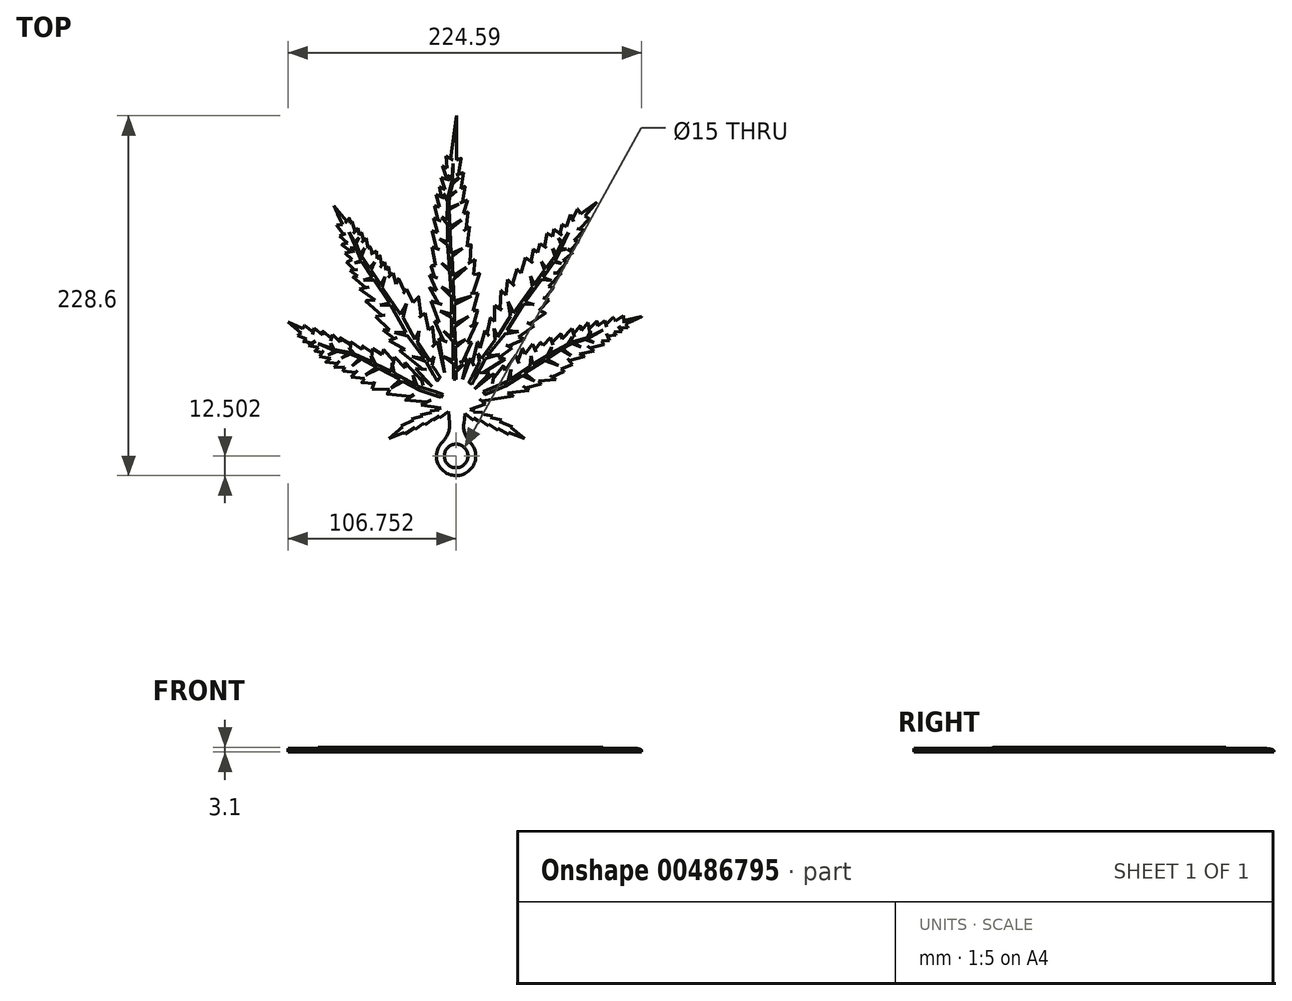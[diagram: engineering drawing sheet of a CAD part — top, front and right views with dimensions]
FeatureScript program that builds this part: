
annotation { "Feature Type Name" : "Feature", "Feature Type Description" : "" }
export const myFeature = defineFeature(function(context is Context, id is Id, definition is map)
    precondition{}
    {
        {
            var Q0;
            Q0=qCreatedBy(makeId("Top.planeOp"),FACE);
            cPlane(context, id + "F0", {"entities" : qUnion([Q0]), "cplaneType" : CPlaneType.OFFSET, "offset" : 2.5 * mm, "width" : 150 * mm, "height" : 150 * mm});
        }
        {
            var Q0;
            Q0=qCreatedBy(makeId("Top.planeOp"),FACE);
            var sketch = newSketch(context, id + "F1", { "sketchPlane" : qUnion([Q0])});
            skLineSegment(sketch, "E0.MirrorCS", {"start": v(-24.15, -17.47) * mm, "end": v(-22.78, -18.23) * mm});
            skLineSegment(sketch, "E1.MirrorCS", {"start": v(-21.88, -22.85) * mm, "end": v(-21.43, -23.84) * mm});
            skLineSegment(sketch, "E2.MirrorCS", {"start": v(-16.34, -20.03) * mm, "end": v(-16.15, -20.85) * mm});
            skLineSegment(sketch, "E3.MirrorCS", {"start": v(-27.7, -25.52) * mm, "end": v(-27.51, -26.67) * mm});
            skLineSegment(sketch, "E4.MirrorCS", {"start": v(-16.15, -20.85) * mm, "end": v(-12.07, -18.38) * mm});
            skLineSegment(sketch, "E5.MirrorCS", {"start": v(-29.84, -20.19) * mm, "end": v(-28.49, -20.94) * mm});
            skLineSegment(sketch, "E6.MirrorCS", {"start": v(-27.51, -26.67) * mm, "end": v(-21.88, -22.85) * mm});
            skLineSegment(sketch, "E7.MirrorCS", {"start": v(-17.1, -16.14) * mm, "end": v(-24.15, -17.47) * mm});
            skLineSegment(sketch, "E8.MirrorCS", {"start": v(93.66, 39.93) * mm, "end": v(93.13, 42.28) * mm});
            skLineSegment(sketch, "E9.MirrorCS", {"start": v(-18.21, -15.02) * mm, "end": v(-17.1, -16.14) * mm});
            skLineSegment(sketch, "E10.MirrorCS", {"start": v(-12.36, -14.52) * mm, "end": v(-18.21, -15.02) * mm});
            skLineSegment(sketch, "E11.MirrorCS", {"start": v(-21.43, -23.84) * mm, "end": v(-16.34, -20.03) * mm});
            skLineSegment(sketch, "E12.MirrorCS", {"start": v(99.9, 33.33) * mm, "end": v(98.7, 35) * mm});
            skLineSegment(sketch, "E13.MirrorCS", {"start": v(-22.78, -18.23) * mm, "end": v(-29.84, -20.19) * mm});
            skLineSegment(sketch, "E14.MirrorCS", {"start": v(9.62, -15.66) * mm, "end": v(10.2, -14.93) * mm});
            skLineSegment(sketch, "E15.MirrorCS", {"start": v(48.5, 23.9) * mm, "end": v(46.84, 27.4) * mm});
            skLineSegment(sketch, "E16.MirrorCS", {"start": v(-8.6, 125.55) * mm, "end": v(-12.12, 127.28) * mm});
            skLineSegment(sketch, "E17.MirrorCS", {"start": v(88.27, 39.04) * mm, "end": v(88, 42) * mm});
            skLineSegment(sketch, "E18.MirrorCS", {"start": v(-12.07, -18.38) * mm, "end": v(-12.07, -19.6) * mm});
            skLineSegment(sketch, "E19.MirrorCS", {"start": v(-44.52, 76.69) * mm, "end": v(-46.07, 74.38) * mm});
            skLineSegment(sketch, "E20.MirrorCS", {"start": v(14.51, -17.11) * mm, "end": v(15.3, -16.07) * mm});
            skLineSegment(sketch, "E21.MirrorCS", {"start": v(-39.89, 65.56) * mm, "end": v(-41.74, 72.67) * mm});
            skLineSegment(sketch, "E22.MirrorCS", {"start": v(93.13, 42.28) * mm, "end": v(88.27, 39.04) * mm});
            skLineSegment(sketch, "E23.MirrorCS", {"start": v(-12.07, -19.6) * mm, "end": v(-6.3, -15.51) * mm});
            skLineSegment(sketch, "E24.MirrorCS", {"start": v(88, 42) * mm, "end": v(82.7, 37.15) * mm});
            skLineSegment(sketch, "E25.MirrorCS", {"start": v(-47.18, 79.6) * mm, "end": v(-48.77, 77.58) * mm});
            skLineSegment(sketch, "E26.MirrorCS", {"start": v(99.75, 42.07) * mm, "end": v(98.19, 44.3) * mm});
            skLineSegment(sketch, "E27.MirrorCS", {"start": v(-63.23, 96.82) * mm, "end": v(-63.82, 101.24) * mm});
            skLineSegment(sketch, "E28.MirrorCS", {"start": v(-12.95, -13.9) * mm, "end": v(-12.36, -14.52) * mm});
            skLineSegment(sketch, "E29.MirrorCS", {"start": v(-67.78, 81.08) * mm, "end": v(-71.02, 79.47) * mm});
            skLineSegment(sketch, "E30.MirrorCS", {"start": v(95.95, 29.74) * mm, "end": v(94.6, 32.57) * mm});
            skLineSegment(sketch, "E31.MirrorCS", {"start": v(98.19, 44.3) * mm, "end": v(93.66, 39.93) * mm});
            skLineSegment(sketch, "E32.MirrorCS", {"start": v(-60.85, 26.35) * mm, "end": v(-61.4, 24) * mm});
            skLineSegment(sketch, "E33.MirrorCS", {"start": v(98.7, 35) * mm, "end": v(103.85, 35.51) * mm});
            skLineSegment(sketch, "E34.MirrorCS", {"start": v(-52.13, 86.53) * mm, "end": v(-54.6, 85.35) * mm});
            skLineSegment(sketch, "E35.MirrorCS", {"start": v(-57.39, 88.4) * mm, "end": v(-58.72, 94.78) * mm});
            skLineSegment(sketch, "E36.MirrorCS", {"start": v(-96.6, 30.56) * mm, "end": v(-98.6, 28.98) * mm});
            skLineSegment(sketch, "E37.MirrorCS", {"start": v(-23.87, -11.37) * mm, "end": v(-7.76, -13.63) * mm});
            skLineSegment(sketch, "E38.MirrorCS", {"start": v(59.47, 28.52) * mm, "end": v(58.4, 31.74) * mm});
            skLineSegment(sketch, "E39.MirrorCS", {"start": v(22.79, 41.65) * mm, "end": v(20.2, 44.17) * mm});
            skLineSegment(sketch, "E40.MirrorCS", {"start": v(-91.93, 37.8) * mm, "end": v(-92.53, 35.19) * mm});
            skLineSegment(sketch, "E41.MirrorCS", {"start": v(-8.17, -11.87) * mm, "end": v(-12.95, -13.9) * mm});
            skLineSegment(sketch, "E42.MirrorCS", {"start": v(94.6, 32.57) * mm, "end": v(99.9, 33.33) * mm});
            skLineSegment(sketch, "E43.MirrorCS", {"start": v(-70.5, 91.5) * mm, "end": v(-74.2, 90.73) * mm});
            skLineSegment(sketch, "E44.MirrorCS", {"start": v(40.63, 24.63) * mm, "end": v(37.6, 16.9) * mm});
            skLineSegment(sketch, "E45.MirrorCS", {"start": v(-67.78, 105.17) * mm, "end": v(-68.8, 104.3) * mm});
            skLineSegment(sketch, "E46.MirrorCS", {"start": v(9.47, -20.96) * mm, "end": v(9.47, -19.45) * mm});
            skLineSegment(sketch, "E47.MirrorCS", {"start": v(-69.45, 107.55) * mm, "end": v(-71.09, 105.54) * mm});
            skLineSegment(sketch, "E48.MirrorCS", {"start": v(107.5, 38.06) * mm, "end": v(106.14, 40.04) * mm});
            skLineSegment(sketch, "E49.MirrorCS", {"start": v(-49.84, 83.5) * mm, "end": v(-51.68, 81.6) * mm});
            skLineSegment(sketch, "E50.MirrorCS", {"start": v(59.63, 95.72) * mm, "end": v(56.23, 97.8) * mm});
            skLineSegment(sketch, "E51.MirrorCS", {"start": v(-11, 121.03) * mm, "end": v(-14.22, 122.51) * mm});
            skLineSegment(sketch, "E52.MirrorCS", {"start": v(-12.12, 127.28) * mm, "end": v(-11, 121.03) * mm});
            skLineSegment(sketch, "E53.MirrorCS", {"start": v(-54.6, 85.35) * mm, "end": v(-56.09, 89.21) * mm});
            skLineSegment(sketch, "E54.MirrorCS", {"start": v(-65.77, 98.92) * mm, "end": v(-67.78, 105.17) * mm});
            skLineSegment(sketch, "E55.MirrorCS", {"start": v(10.2, -14.93) * mm, "end": v(5.27, -13.6) * mm});
            skLineSegment(sketch, "E56.MirrorCS", {"start": v(-46.07, 74.38) * mm, "end": v(-47.18, 79.6) * mm});
            skLineSegment(sketch, "E57.MirrorCS", {"start": v(53.77, 26.64) * mm, "end": v(52.16, 28.56) * mm});
            skLineSegment(sketch, "E58.MirrorCS", {"start": v(-79.9, 33.62) * mm, "end": v(-80.8, 30.9) * mm});
            skLineSegment(sketch, "E59.MirrorCS", {"start": v(33.94, 24.96) * mm, "end": v(31.73, 26.08) * mm});
            skLineSegment(sketch, "E60.MirrorCS", {"start": v(-68.18, 86.24) * mm, "end": v(-72.2, 85.35) * mm});
            skLineSegment(sketch, "E61.MirrorCS", {"start": v(-63.82, 101.24) * mm, "end": v(-65.77, 98.92) * mm});
            skLineSegment(sketch, "E62.MirrorCS", {"start": v(36.08, 20.08) * mm, "end": v(29.34, 10.62) * mm});
            skLineSegment(sketch, "E63.MirrorCS", {"start": v(-54.6, 24.71) * mm, "end": v(-54.85, 22.2) * mm});
            skLineSegment(sketch, "E64.MirrorCS", {"start": v(52.16, 28.56) * mm, "end": v(48.5, 23.9) * mm});
            skLineSegment(sketch, "E65.MirrorCS", {"start": v(-61.69, 98.18) * mm, "end": v(-63.23, 96.82) * mm});
            skLineSegment(sketch, "E66.MirrorCS", {"start": v(-54.85, 22.2) * mm, "end": v(-60.85, 26.35) * mm});
            skLineSegment(sketch, "E67.MirrorCS", {"start": v(-68.77, 28.98) * mm, "end": v(-68.77, 27) * mm});
            skLineSegment(sketch, "E68.MirrorCS", {"start": v(-68.77, 27) * mm, "end": v(-75.14, 31.33) * mm});
            skLineSegment(sketch, "E69.MirrorCS", {"start": v(11.68, 41.54) * mm, "end": v(9.37, 39.84) * mm});
            skLineSegment(sketch, "E70.MirrorCS", {"start": v(-10.18, 140.6) * mm, "end": v(-7.4, 132) * mm});
            skLineSegment(sketch, "E71.MirrorCS", {"start": v(-77.58, 102.97) * mm, "end": v(-73.13, 97.13) * mm});
            skLineSegment(sketch, "E72.MirrorCS", {"start": v(90.7, 29.27) * mm, "end": v(95.95, 29.74) * mm});
            skLineSegment(sketch, "E73.MirrorCS", {"start": v(-92.53, 35.19) * mm, "end": v(-97.83, 39.3) * mm});
            skLineSegment(sketch, "E74.MirrorCS", {"start": v(-74.2, 90.73) * mm, "end": v(-68.18, 86.24) * mm});
            skLineSegment(sketch, "E75.MirrorCS", {"start": v(15.3, -16.07) * mm, "end": v(9.62, -15.66) * mm});
            skLineSegment(sketch, "E76.MirrorCS", {"start": v(-71.02, 79.47) * mm, "end": v(-65.98, 74.5) * mm});
            skLineSegment(sketch, "E77.MirrorCS", {"start": v(25.29, 18.6) * mm, "end": v(33.94, 24.96) * mm});
            skLineSegment(sketch, "E78.MirrorCS", {"start": v(-72.42, 13.02) * mm, "end": v(-73.31, 10.43) * mm});
            skLineSegment(sketch, "E79.MirrorCS", {"start": v(17.11, -10.61) * mm, "end": v(14.83, -8.82) * mm});
            skLineSegment(sketch, "E80.MirrorCS", {"start": v(5.69, 28.31) * mm, "end": v(11.68, 41.54) * mm});
            skLineSegment(sketch, "E81.MirrorCS", {"start": v(-86.3, 35.6) * mm, "end": v(-86.3, 33.25) * mm});
            skLineSegment(sketch, "E82.MirrorCS", {"start": v(31.73, -30.06) * mm, "end": v(31.73, -28.66) * mm});
            skLineSegment(sketch, "E83.MirrorCS", {"start": v(-48.77, 77.58) * mm, "end": v(-49.84, 83.5) * mm});
            skLineSegment(sketch, "E84.MirrorCS", {"start": v(-60.45, 93.14) * mm, "end": v(-61.69, 98.18) * mm});
            skLineSegment(sketch, "E85.MirrorCS", {"start": v(-72.2, 85.35) * mm, "end": v(-67.78, 81.08) * mm});
            skLineSegment(sketch, "E86.MirrorCS", {"start": v(-58.72, 94.78) * mm, "end": v(-60.45, 93.14) * mm});
            skLineSegment(sketch, "E87.MirrorCS", {"start": v(68.4, 102.12) * mm, "end": v(65.63, 103.44) * mm});
            skLineSegment(sketch, "E88.MirrorCS", {"start": v(13.63, 24.96) * mm, "end": v(12.05, 28.76) * mm});
            skLineSegment(sketch, "E89.MirrorCS", {"start": v(3.97, -16.71) * mm, "end": v(9.47, -20.96) * mm});
            skLineSegment(sketch, "E90.MirrorCS", {"start": v(29.98, 58.7) * mm, "end": v(27, 61.6) * mm});
            skLineSegment(sketch, "E91.MirrorCS", {"start": v(25.17, -27.3) * mm, "end": v(25.17, -26.06) * mm});
            skLineSegment(sketch, "E92.MirrorCS", {"start": v(8.17, 28.54) * mm, "end": v(5.69, 28.31) * mm});
            skLineSegment(sketch, "E93.MirrorCS", {"start": v(82.06, 41.17) * mm, "end": v(78.05, 36.06) * mm});
            skLineSegment(sketch, "E94.MirrorCS", {"start": v(-102.13, 32.87) * mm, "end": v(-96.6, 30.56) * mm});
            skLineSegment(sketch, "E95.MirrorCS", {"start": v(-92.6, 28.2) * mm, "end": v(-95.33, 26.41) * mm});
            skLineSegment(sketch, "E96.MirrorCS", {"start": v(103.85, 35.51) * mm, "end": v(102.4, 37.6) * mm});
            skLineSegment(sketch, "E97.MirrorCS", {"start": v(5.1, -14.93) * mm, "end": v(17.11, -10.61) * mm});
            skLineSegment(sketch, "E98.MirrorCS", {"start": v(-43.42, 70.95) * mm, "end": v(-44.52, 76.69) * mm});
            skLineSegment(sketch, "E99.MirrorCS", {"start": v(105, 42.33) * mm, "end": v(104.7, 45.51) * mm});
            skLineSegment(sketch, "E100.MirrorCS", {"start": v(29.4, 17.98) * mm, "end": v(25.29, 18.6) * mm});
            skLineSegment(sketch, "E101.MirrorCS", {"start": v(-73.68, 103.44) * mm, "end": v(-77.58, 102.97) * mm});
            skLineSegment(sketch, "E102.MirrorCS", {"start": v(-98.6, 28.98) * mm, "end": v(-92.6, 28.2) * mm});
            skLineSegment(sketch, "E103.MirrorCS", {"start": v(41.92, 30.66) * mm, "end": v(38, 31.83) * mm});
            skLineSegment(sketch, "E104.MirrorCS", {"start": v(-75.14, 31.33) * mm, "end": v(-75.14, 28.8) * mm});
            skLineSegment(sketch, "E105.MirrorCS", {"start": v(-7.4, 132) * mm, "end": v(-11, 133.1) * mm});
            skLineSegment(sketch, "E106.MirrorCS", {"start": v(-61.4, 24) * mm, "end": v(-68.77, 28.98) * mm});
            skLineSegment(sketch, "E107.MirrorCS", {"start": v(58.4, 31.74) * mm, "end": v(53.77, 26.64) * mm});
            skLineSegment(sketch, "E108.MirrorCS", {"start": v(42.32, 21.07) * mm, "end": v(40.63, 24.63) * mm});
            skLineSegment(sketch, "E109.MirrorCS", {"start": v(28.53, 13.78) * mm, "end": v(21.92, 5.35) * mm});
            skLineSegment(sketch, "E110.MirrorCS", {"start": v(-56.09, 89.21) * mm, "end": v(-57.39, 88.4) * mm});
            skLineSegment(sketch, "E111.MirrorCS", {"start": v(-97.83, 39.3) * mm, "end": v(-99, 37.2) * mm});
            skLineSegment(sketch, "E112.MirrorCS", {"start": v(52.48, 1.92) * mm, "end": v(50.7, 3.95) * mm});
            skLineSegment(sketch, "E113.MirrorCS", {"start": v(65.67, 30.69) * mm, "end": v(65.11, 34.03) * mm});
            skLineSegment(sketch, "E114.MirrorCS", {"start": v(13.63, -22.05) * mm, "end": v(13.63, -20.86) * mm});
            skLineSegment(sketch, "E115.MirrorCS", {"start": v(51.56, 91.44) * mm, "end": v(50.07, 85.48) * mm});
            skLineSegment(sketch, "E116.MirrorCS", {"start": v(-75.57, 96.08) * mm, "end": v(-70.5, 91.5) * mm});
            skLineSegment(sketch, "E117.MirrorCS", {"start": v(-65.98, 74.5) * mm, "end": v(-69.01, 74.15) * mm});
            skLineSegment(sketch, "E118.MirrorCS", {"start": v(-11, 133.1) * mm, "end": v(-8.6, 125.55) * mm});
            skLineSegment(sketch, "E119.MirrorCS", {"start": v(18.12, 34.15) * mm, "end": v(16.76, 35.99) * mm});
            skLineSegment(sketch, "E120.MirrorCS", {"start": v(-69.01, 74.15) * mm, "end": v(-64.31, 70.63) * mm});
            skLineSegment(sketch, "E121.MirrorCS", {"start": v(16.76, 35.99) * mm, "end": v(13.63, 24.96) * mm});
            skLineSegment(sketch, "E122.MirrorCS", {"start": v(92.2, 27.09) * mm, "end": v(90.7, 29.27) * mm});
            skLineSegment(sketch, "E123.MirrorCS", {"start": v(3.1, 136.52) * mm, "end": v(0, 135.44) * mm});
            skLineSegment(sketch, "E124.MirrorCS", {"start": v(-23.87, 6.72) * mm, "end": v(-23.28, 4.09) * mm});
            skLineSegment(sketch, "E125.MirrorCS", {"start": v(-40.6, 19.11) * mm, "end": v(-41.19, 16.58) * mm});
            skLineSegment(sketch, "E126.MirrorCS", {"start": v(65.11, 34.03) * mm, "end": v(59.47, 28.52) * mm});
            skLineSegment(sketch, "E127.MirrorCS", {"start": v(-73.13, 97.13) * mm, "end": v(-75.57, 96.08) * mm});
            skLineSegment(sketch, "E128.MirrorCS", {"start": v(13.63, -20.86) * mm, "end": v(19.14, -24.6) * mm});
            skLineSegment(sketch, "E129.MirrorCS", {"start": v(6.96, 102.1) * mm, "end": v(4.66, 100.42) * mm});
            skLineSegment(sketch, "E130.MirrorCS", {"start": v(29.34, 10.62) * mm, "end": v(28.53, 13.78) * mm});
            skLineSegment(sketch, "E131.MirrorCS", {"start": v(21.43, -18.36) * mm, "end": v(14.51, -17.11) * mm});
            skLineSegment(sketch, "E132.MirrorCS", {"start": v(66.98, 10.14) * mm, "end": v(65, 11.7) * mm});
            skLineSegment(sketch, "E133.MirrorCS", {"start": v(19.14, -24.6) * mm, "end": v(19.14, -23.46) * mm});
            skLineSegment(sketch, "E134.MirrorCS", {"start": v(5.67, 18) * mm, "end": v(2.68, 16.58) * mm});
            skLineSegment(sketch, "E135.MirrorCS", {"start": v(82.7, 37.15) * mm, "end": v(82.06, 41.17) * mm});
            skLineSegment(sketch, "E136.MirrorCS", {"start": v(-41.74, 72.67) * mm, "end": v(-43.42, 70.95) * mm});
            skLineSegment(sketch, "E137.MirrorCS", {"start": v(-36.67, -24.67) * mm, "end": v(-35.58, -25.13) * mm});
            skLineSegment(sketch, "E138.MirrorCS", {"start": v(-51.68, 81.6) * mm, "end": v(-52.13, 86.53) * mm});
            skLineSegment(sketch, "E139.MirrorCS", {"start": v(-100.03, 34.51) * mm, "end": v(-102.13, 32.87) * mm});
            skLineSegment(sketch, "E140.MirrorCS", {"start": v(102.4, 37.6) * mm, "end": v(107.5, 38.06) * mm});
            skLineSegment(sketch, "E141.MirrorCS", {"start": v(-91.28, 23.17) * mm, "end": v(-86.57, 22.07) * mm});
            skLineSegment(sketch, "E142.MirrorCS", {"start": v(-68.8, 104.3) * mm, "end": v(-69.45, 107.55) * mm});
            skLineSegment(sketch, "E143.MirrorCS", {"start": v(37.6, 16.9) * mm, "end": v(36.08, 20.08) * mm});
            skLineSegment(sketch, "E144.MirrorCS", {"start": v(46.84, 27.4) * mm, "end": v(42.32, 21.07) * mm});
            skLineSegment(sketch, "E145.MirrorCS", {"start": v(22.38, 8.77) * mm, "end": v(10.23, -1.16) * mm});
            skLineSegment(sketch, "E146.MirrorCS", {"start": v(-86.3, 33.25) * mm, "end": v(-91.93, 37.8) * mm});
            skLineSegment(sketch, "E147.MirrorCS", {"start": v(9.47, -19.45) * mm, "end": v(13.63, -22.05) * mm});
            skLineSegment(sketch, "E148.MirrorCS", {"start": v(-38.24, 69.03) * mm, "end": v(-39.89, 65.56) * mm});
            skLineSegment(sketch, "E149.MirrorCS", {"start": v(20.2, 44.17) * mm, "end": v(18.12, 34.15) * mm});
            skLineSegment(sketch, "E150.MirrorCS", {"start": v(-7.4, 139.14) * mm, "end": v(-10.18, 140.6) * mm});
            skLineSegment(sketch, "E151.MirrorCS", {"start": v(25.17, -26.06) * mm, "end": v(31.73, -30.06) * mm});
            skLineSegment(sketch, "E152.MirrorCS", {"start": v(12.09, 48.84) * mm, "end": v(9.17, 48.57) * mm});
            skLineSegment(sketch, "E153.MirrorCS", {"start": v(15.98, 9.26) * mm, "end": v(29.4, 17.98) * mm});
            skLineSegment(sketch, "E154.MirrorCS", {"start": v(2.47, 117.56) * mm, "end": v(3.97, 127.56) * mm});
            skLineSegment(sketch, "E155.MirrorCS", {"start": v(-21.21, 47.13) * mm, "end": v(-23.82, 45.38) * mm});
            skLineSegment(sketch, "E156.MirrorCS", {"start": v(26.28, 49.81) * mm, "end": v(22.79, 51.85) * mm});
            skLineSegment(sketch, "E157.MirrorCS", {"start": v(-16.85, 0.38) * mm, "end": v(-23.87, 6.72) * mm});
            skLineSegment(sketch, "E158.MirrorCS", {"start": v(34.27, 65.55) * mm, "end": v(31.05, 68.4) * mm});
            skLineSegment(sketch, "E159.MirrorCS", {"start": v(-28.83, 53.9) * mm, "end": v(-32.94, 62.51) * mm});
            skLineSegment(sketch, "E160.MirrorCS", {"start": v(-73.31, 10.43) * mm, "end": v(-65.4, 9.25) * mm});
            skLineSegment(sketch, "E161.MirrorCS", {"start": v(-86.57, 22.07) * mm, "end": v(-88.4, 19.6) * mm});
            skLineSegment(sketch, "E162.MirrorCS", {"start": v(-47.74, 23.88) * mm, "end": v(-48.46, 20.77) * mm});
            skLineSegment(sketch, "E163.MirrorCS", {"start": v(-33.98, -8.19) * mm, "end": v(-20, -9.36) * mm});
            skLineSegment(sketch, "E164.MirrorCS", {"start": v(-23.07, 11.66) * mm, "end": v(-27.33, 12.06) * mm});
            skLineSegment(sketch, "E165.MirrorCS", {"start": v(-33.89, 12.31) * mm, "end": v(-40.6, 19.11) * mm});
            skLineSegment(sketch, "E166.MirrorCS", {"start": v(-65.4, 9.25) * mm, "end": v(-68.18, 6.5) * mm});
            skLineSegment(sketch, "E167.MirrorCS", {"start": v(3.11, 110.24) * mm, "end": v(5.7, 118.81) * mm});
            skLineSegment(sketch, "E168.MirrorCS", {"start": v(3.97, 127.56) * mm, "end": v(1.62, 126.1) * mm});
            skLineSegment(sketch, "E169.MirrorCS", {"start": v(50.07, 85.48) * mm, "end": v(47.52, 87.8) * mm});
            skLineSegment(sketch, "E170.MirrorCS", {"start": v(44.67, -2.08) * mm, "end": v(42.5, -0.38) * mm});
            skLineSegment(sketch, "E171.MirrorCS", {"start": v(-16.45, 38.32) * mm, "end": v(-19.14, 36.51) * mm});
            skLineSegment(sketch, "E172.MirrorCS", {"start": v(-76.74, 15.22) * mm, "end": v(-79, 12.65) * mm});
            skLineSegment(sketch, "E173.MirrorCS", {"start": v(27.36, -20.86) * mm, "end": v(20.18, -19.09) * mm});
            skLineSegment(sketch, "E174.MirrorCS", {"start": v(68.98, 79.6) * mm, "end": v(66.29, 80.47) * mm});
            skLineSegment(sketch, "E175.MirrorCS", {"start": v(55.25, 47.14) * mm, "end": v(51.2, 48.65) * mm});
            skLineSegment(sketch, "E176.MirrorCS", {"start": v(-48.46, 20.77) * mm, "end": v(-54.6, 24.71) * mm});
            skLineSegment(sketch, "E177.MirrorCS", {"start": v(20.18, -19.09) * mm, "end": v(21.43, -18.36) * mm});
            skLineSegment(sketch, "E178.MirrorCS", {"start": v(-68.18, 6.5) * mm, "end": v(-59.86, 5.45) * mm});
            skLineSegment(sketch, "E179.MirrorCS", {"start": v(-35.58, -25.13) * mm, "end": v(-44.13, -32.65) * mm});
            skLineSegment(sketch, "E180.MirrorCS", {"start": v(72.28, 106.83) * mm, "end": v(70.94, 109.64) * mm});
            skLineSegment(sketch, "E181.MirrorCS", {"start": v(5.7, 118.81) * mm, "end": v(2.47, 117.56) * mm});
            skLineSegment(sketch, "E182.MirrorCS", {"start": v(47.8, 39.04) * mm, "end": v(45.05, 40.27) * mm});
            skLineSegment(sketch, "E183.MirrorCS", {"start": v(-25.42, 57.4) * mm, "end": v(-28.83, 53.9) * mm});
            skLineSegment(sketch, "E184.MirrorCS", {"start": v(-62.86, 62.53) * mm, "end": v(-53.06, 55.5) * mm});
            skLineSegment(sketch, "E185.MirrorCS", {"start": v(-95.33, 26.41) * mm, "end": v(-88.8, 25.33) * mm});
            skLineSegment(sketch, "E186.MirrorCS", {"start": v(-80.8, 30.9) * mm, "end": v(-86.3, 35.6) * mm});
            skLineSegment(sketch, "E187.MirrorCS", {"start": v(77.45, 39.22) * mm, "end": v(73.1, 33.68) * mm});
            skLineSegment(sketch, "E188.MirrorCS", {"start": v(25.95, -21.59) * mm, "end": v(27.36, -20.86) * mm});
            skLineSegment(sketch, "E189.MirrorCS", {"start": v(7.55, 18.58) * mm, "end": v(2.49, 4.84) * mm});
            skLineSegment(sketch, "E190.MirrorCS", {"start": v(-13.87, 61.56) * mm, "end": v(-18.49, 63.2) * mm});
            skLineSegment(sketch, "E191.MirrorCS", {"start": v(-59.86, 5.45) * mm, "end": v(-61.56, 2.91) * mm});
            skLineSegment(sketch, "E192.MirrorCS", {"start": v(-84.35, 15.96) * mm, "end": v(-76.74, 15.22) * mm});
            skLineSegment(sketch, "E193.MirrorCS", {"start": v(12.3, 60) * mm, "end": v(9.14, 59.7) * mm});
            skLineSegment(sketch, "E194.MirrorCS", {"start": v(42.5, -0.38) * mm, "end": v(52.48, 1.92) * mm});
            skLineSegment(sketch, "E195.MirrorCS", {"start": v(-23.28, 4.09) * mm, "end": v(-33.89, 15.87) * mm});
            skLineSegment(sketch, "E196.MirrorCS", {"start": v(-88.8, 25.33) * mm, "end": v(-91.28, 23.17) * mm});
            skLineSegment(sketch, "E197.MirrorCS", {"start": v(104.7, 45.51) * mm, "end": v(99.75, 42.07) * mm});
            skLineSegment(sketch, "E198.MirrorCS", {"start": v(5.26, 89.45) * mm, "end": v(6.96, 102.1) * mm});
            skLineSegment(sketch, "E199.MirrorCS", {"start": v(83.46, 24.96) * mm, "end": v(92.2, 27.09) * mm});
            skLineSegment(sketch, "E200.MirrorCS", {"start": v(77.58, 110.01) * mm, "end": v(75.57, 113.28) * mm});
            skLineSegment(sketch, "E201.MirrorCS", {"start": v(-53.83, 2.26) * mm, "end": v(-55.1, -1.14) * mm});
            skLineSegment(sketch, "E202.MirrorCS", {"start": v(-64.31, 70.63) * mm, "end": v(-67.1, 69.89) * mm});
            skLineSegment(sketch, "E203.MirrorCS", {"start": v(83.02, 107.03) * mm, "end": v(80.39, 108.61) * mm});
            skLineSegment(sketch, "E204.MirrorCS", {"start": v(31.73, 26.08) * mm, "end": v(41.92, 30.66) * mm});
            skLineSegment(sketch, "E205.MirrorCS", {"start": v(21.92, 5.35) * mm, "end": v(22.38, 8.77) * mm});
            skLineSegment(sketch, "E206.MirrorCS", {"start": v(1.58, 145.3) * mm, "end": v(-1.24, 144.46) * mm});
            skLineSegment(sketch, "E207.MirrorCS", {"start": v(19.72, 8.98) * mm, "end": v(15.98, 9.26) * mm});
            skLineSegment(sketch, "E208.MirrorCS", {"start": v(41.92, -32.5) * mm, "end": v(33.29, -25.59) * mm});
            skLineSegment(sketch, "E209.MirrorCS", {"start": v(73.1, 33.68) * mm, "end": v(71.98, 37.4) * mm});
            skLineSegment(sketch, "E210.MirrorCS", {"start": v(9.37, 39.84) * mm, "end": v(12.09, 48.84) * mm});
            skLineSegment(sketch, "E211.MirrorCS", {"start": v(-61.56, 2.91) * mm, "end": v(-53.83, 2.26) * mm});
            skLineSegment(sketch, "E212.MirrorCS", {"start": v(33.29, -25.59) * mm, "end": v(34.27, -25.12) * mm});
            skLineSegment(sketch, "E213.MirrorCS", {"start": v(70.94, 109.64) * mm, "end": v(68.4, 102.12) * mm});
            skLineSegment(sketch, "E214.MirrorCS", {"start": v(47.52, 87.8) * mm, "end": v(46.04, 79.83) * mm});
            skLineSegment(sketch, "E215.MirrorCS", {"start": v(54.56, 89.43) * mm, "end": v(51.56, 91.44) * mm});
            skLineSegment(sketch, "E216.MirrorCS", {"start": v(-33.95, 24) * mm, "end": v(-37.32, 23.17) * mm});
            skLineSegment(sketch, "E217.MirrorCS", {"start": v(42.57, 82.4) * mm, "end": v(39.54, 72.43) * mm});
            skLineSegment(sketch, "E218.MirrorCS", {"start": v(2.49, 4.84) * mm, "end": v(5.67, 18) * mm});
            skLineSegment(sketch, "E219.MirrorCS", {"start": v(10.23, -1.16) * mm, "end": v(19.72, 8.98) * mm});
            skLineSegment(sketch, "E220.MirrorCS", {"start": v(65.63, 103.44) * mm, "end": v(64.36, 97.41) * mm});
            skLineSegment(sketch, "E221.MirrorCS", {"start": v(-33.89, 15.87) * mm, "end": v(-33.89, 12.31) * mm});
            skLineSegment(sketch, "E222.MirrorCS", {"start": v(0, 135.44) * mm, "end": v(1.58, 145.3) * mm});
            skLineSegment(sketch, "E223.MirrorCS", {"start": v(22.79, 51.85) * mm, "end": v(22.79, 41.65) * mm});
            skLineSegment(sketch, "E224.MirrorCS", {"start": v(4.66, 100.42) * mm, "end": v(5.9, 111.27) * mm});
            skLineSegment(sketch, "E225.MirrorCS", {"start": v(-16.82, 89.06) * mm, "end": v(-14.72, 77.37) * mm});
            skLineSegment(sketch, "E226.MirrorCS", {"start": v(-30.27, -5.9) * mm, "end": v(-33.98, -8.19) * mm});
            skLineSegment(sketch, "E227.MirrorCS", {"start": v(79.64, 99.96) * mm, "end": v(76.93, 100.42) * mm});
            skLineSegment(sketch, "E228.MirrorCS", {"start": v(60.34, 63.26) * mm, "end": v(57.01, 63.84) * mm});
            skLineSegment(sketch, "E229.MirrorCS", {"start": v(56.23, 97.8) * mm, "end": v(54.56, 89.43) * mm});
            skLineSegment(sketch, "E230.MirrorCS", {"start": v(-13.91, 88.07) * mm, "end": v(-16.82, 89.06) * mm});
            skLineSegment(sketch, "E231.MirrorCS", {"start": v(-44.13, -32.65) * mm, "end": v(-34.52, -28.58) * mm});
            skLineSegment(sketch, "E232.MirrorCS", {"start": v(-79, 12.65) * mm, "end": v(-72.42, 13.02) * mm});
            skLineSegment(sketch, "E233.MirrorCS", {"start": v(-14.22, 122.51) * mm, "end": v(-12, 114.41) * mm});
            skLineSegment(sketch, "E234.MirrorCS", {"start": v(-88.4, 19.6) * mm, "end": v(-81.38, 18.25) * mm});
            skLineSegment(sketch, "E235.MirrorCS", {"start": v(-28.49, -20.94) * mm, "end": v(-36.67, -24.67) * mm});
            skLineSegment(sketch, "E236.MirrorCS", {"start": v(-27.33, 12.06) * mm, "end": v(-16.85, 0.38) * mm});
            skLineSegment(sketch, "E237.MirrorCS", {"start": v(2.68, 16.58) * mm, "end": v(8.17, 28.54) * mm});
            skLineSegment(sketch, "E238.MirrorCS", {"start": v(-19.14, 36.51) * mm, "end": v(-21.21, 47.13) * mm});
            skLineSegment(sketch, "E239.MirrorCS", {"start": v(8.9, 15.74) * mm, "end": v(7.55, 18.58) * mm});
            skLineSegment(sketch, "E240.MirrorCS", {"start": v(-15.34, 42) * mm, "end": v(-9.48, 29.7) * mm});
            skLineSegment(sketch, "E241.MirrorCS", {"start": v(-37.32, 23.17) * mm, "end": v(-23.07, 11.66) * mm});
            skLineSegment(sketch, "E242.MirrorCS", {"start": v(-41.19, 16.58) * mm, "end": v(-47.74, 23.88) * mm});
            skLineSegment(sketch, "E243.MirrorCS", {"start": v(1.62, 126.1) * mm, "end": v(3.1, 136.52) * mm});
            skLineSegment(sketch, "E244.MirrorCS", {"start": v(-34.3, 60.78) * mm, "end": v(-38.24, 69.03) * mm});
            skLineSegment(sketch, "E245.MirrorCS", {"start": v(7.99, 90.57) * mm, "end": v(5.26, 89.45) * mm});
            skLineSegment(sketch, "E246.MirrorCS", {"start": v(-5.06, 145.09) * mm, "end": v(-7.99, 146.98) * mm});
            skLineSegment(sketch, "E247.MirrorCS", {"start": v(5.9, 111.27) * mm, "end": v(3.11, 110.24) * mm});
            skLineSegment(sketch, "E248.MirrorCS", {"start": v(-17.42, 77.12) * mm, "end": v(-15.21, 70.07) * mm});
            skLineSegment(sketch, "E249.MirrorCS", {"start": v(38, 31.83) * mm, "end": v(47.8, 39.04) * mm});
            skLineSegment(sketch, "E250.MirrorCS", {"start": v(75.57, 113.28) * mm, "end": v(72.28, 106.83) * mm});
            skLineSegment(sketch, "E251.MirrorCS", {"start": v(-58.97, 63.2) * mm, "end": v(-62.86, 62.53) * mm});
            skLineSegment(sketch, "E252.MirrorCS", {"start": v(39.54, 72.43) * mm, "end": v(37.07, 75.15) * mm});
            skLineSegment(sketch, "E253.MirrorCS", {"start": v(31.05, 68.4) * mm, "end": v(29.98, 58.7) * mm});
            skLineSegment(sketch, "E254.MirrorCS", {"start": v(61.73, 4.78) * mm, "end": v(59.47, 6.56) * mm});
            skLineSegment(sketch, "E255.MirrorCS", {"start": v(-81.38, 18.25) * mm, "end": v(-84.35, 15.96) * mm});
            skLineSegment(sketch, "E256.MirrorCS", {"start": v(-43.97, 36.21) * mm, "end": v(-47.96, 36.21) * mm});
            skLineSegment(sketch, "E257.MirrorCS", {"start": v(-32.94, 62.51) * mm, "end": v(-34.3, 60.78) * mm});
            skLineSegment(sketch, "E258.MirrorCS", {"start": v(31.73, -28.66) * mm, "end": v(41.92, -32.5) * mm});
            skLineSegment(sketch, "E259.MirrorCS", {"start": v(9.17, 48.57) * mm, "end": v(12.3, 60) * mm});
            skLineSegment(sketch, "E260.MirrorCS", {"start": v(-7.99, 146.98) * mm, "end": v(-7.4, 139.14) * mm});
            skLineSegment(sketch, "E261.MirrorCS", {"start": v(-75.14, 28.8) * mm, "end": v(-79.9, 33.62) * mm});
            skLineSegment(sketch, "E262.MirrorCS", {"start": v(78.05, 36.06) * mm, "end": v(77.45, 39.22) * mm});
            skLineSegment(sketch, "E263.MirrorCS", {"start": v(65, 11.7) * mm, "end": v(72.5, 14.5) * mm});
            skLineSegment(sketch, "E264.MirrorCS", {"start": v(-67.1, 69.89) * mm, "end": v(-58.97, 63.2) * mm});
            skLineSegment(sketch, "E265.MirrorCS", {"start": v(-16.82, 99.32) * mm, "end": v(-13.91, 88.07) * mm});
            skLineSegment(sketch, "E266.MirrorCS", {"start": v(12.05, 28.76) * mm, "end": v(8.9, 15.74) * mm});
            skLineSegment(sketch, "E267.MirrorCS", {"start": v(76.93, 100.42) * mm, "end": v(83.02, 107.03) * mm});
            skLineSegment(sketch, "E268.MirrorCS", {"start": v(27, 61.6) * mm, "end": v(26.28, 49.81) * mm});
            skLineSegment(sketch, "E269.MirrorCS", {"start": v(19.14, -23.46) * mm, "end": v(25.17, -27.3) * mm});
            skLineSegment(sketch, "E270.MirrorCS", {"start": v(-20, -9.36) * mm, "end": v(-23.87, -11.37) * mm});
            skLineSegment(sketch, "E271.MirrorCS", {"start": v(46.04, 79.83) * mm, "end": v(42.57, 82.4) * mm});
            skLineSegment(sketch, "E272.MirrorCS", {"start": v(-12.55, 41) * mm, "end": v(-15.34, 42) * mm});
            skLineSegment(sketch, "E273.MirrorCS", {"start": v(60.72, 100.42) * mm, "end": v(59.63, 95.72) * mm});
            skLineSegment(sketch, "E274.MirrorCS", {"start": v(-99, 37.2) * mm, "end": v(-108.35, 41.44) * mm});
            skLineSegment(sketch, "E275.MirrorCS", {"start": v(59.47, 6.56) * mm, "end": v(66.98, 10.14) * mm});
            skLineSegment(sketch, "E276.MirrorCS", {"start": v(72.5, 14.5) * mm, "end": v(70.31, 16.9) * mm});
            skLineSegment(sketch, "E277.MirrorCS", {"start": v(-108.35, 41.44) * mm, "end": v(-100.03, 34.51) * mm});
            skLineSegment(sketch, "E278.MirrorCS", {"start": v(34.27, -25.12) * mm, "end": v(25.95, -21.59) * mm});
            skLineSegment(sketch, "E279.MirrorCS", {"start": v(-12, 114.41) * mm, "end": v(-15.15, 115.22) * mm});
            skLineSegment(sketch, "E280.MirrorCS", {"start": v(-33.86, -29.61) * mm, "end": v(-27.7, -25.52) * mm});
            skLineSegment(sketch, "E281.MirrorCS", {"start": v(-34.52, -28.58) * mm, "end": v(-33.86, -29.61) * mm});
            skLineSegment(sketch, "E282.MirrorCS", {"start": v(71.98, 37.4) * mm, "end": v(65.67, 30.69) * mm});
            skLineSegment(sketch, "E283.MirrorCS", {"start": v(-40.85, 31.02) * mm, "end": v(-44.15, 29.78) * mm});
            skLineSegment(sketch, "E284.MirrorCS", {"start": v(-12.61, 53.25) * mm, "end": v(-17.38, 54.74) * mm});
            skLineSegment(sketch, "E285.MirrorCS", {"start": v(-12.5, 31.05) * mm, "end": v(-8.78, 9.26) * mm});
            skLineSegment(sketch, "E286.MirrorCS", {"start": v(-15.4, 26.91) * mm, "end": v(-16.45, 38.32) * mm});
            skLineSegment(sketch, "E287.MirrorCS", {"start": v(-18.49, 63.2) * mm, "end": v(-12.61, 53.25) * mm});
            skLineSegment(sketch, "E288.MirrorCS", {"start": v(-15.21, 70.07) * mm, "end": v(-18.49, 71.25) * mm});
            skLineSegment(sketch, "E289.MirrorCS", {"start": v(-13.42, 28.95) * mm, "end": v(-15.4, 26.91) * mm});
            skLineSegment(sketch, "E290.MirrorCS", {"start": v(65.36, 72.4) * mm, "end": v(62.36, 72.4) * mm});
            skLineSegment(sketch, "E291.MirrorCS", {"start": v(50.7, 3.95) * mm, "end": v(61.73, 4.78) * mm});
            skLineSegment(sketch, "E292.MirrorCS", {"start": v(57.41, 55.3) * mm, "end": v(54.9, 56.35) * mm});
            skLineSegment(sketch, "E293.MirrorCS", {"start": v(-14.72, 77.37) * mm, "end": v(-17.42, 77.12) * mm});
            skLineSegment(sketch, "E294.MirrorCS", {"start": v(76.17, 92.67) * mm, "end": v(73.18, 93.34) * mm});
            skLineSegment(sketch, "E295.MirrorCS", {"start": v(-13.3, 98.21) * mm, "end": v(-16.82, 99.32) * mm});
            skLineSegment(sketch, "E296.MirrorCS", {"start": v(72.78, 85.67) * mm, "end": v(70.62, 86.97) * mm});
            skLineSegment(sketch, "E297.MirrorCS", {"start": v(-15.15, 115.22) * mm, "end": v(-12.99, 106.31) * mm});
            skLineSegment(sketch, "E298.MirrorCS", {"start": v(70.31, 16.9) * mm, "end": v(79.88, 19.65) * mm});
            skLineSegment(sketch, "E299.MirrorCS", {"start": v(-17.38, 54.74) * mm, "end": v(-12.55, 41) * mm});
            skLineSegment(sketch, "E300.MirrorCS", {"start": v(-44.15, 29.78) * mm, "end": v(-33.95, 24) * mm});
            skLineSegment(sketch, "E301.MirrorCS", {"start": v(70.62, 86.97) * mm, "end": v(76.17, 92.67) * mm});
            skLineSegment(sketch, "E302.MirrorCS", {"start": v(106.14, 40.04) * mm, "end": v(116.24, 44.85) * mm});
            skLineSegment(sketch, "E303.MirrorCS", {"start": v(-52.87, 45.06) * mm, "end": v(-43.97, 36.21) * mm});
            skLineSegment(sketch, "E304.MirrorCS", {"start": v(73.18, 93.34) * mm, "end": v(79.64, 99.96) * mm});
            skLineSegment(sketch, "E305.MirrorCS", {"start": v(-15.83, 107.43) * mm, "end": v(-13.3, 98.21) * mm});
            skLineSegment(sketch, "E306.MirrorCS", {"start": v(-23.82, 45.38) * mm, "end": v(-25.42, 57.4) * mm});
            skLineSegment(sketch, "E307.MirrorCS", {"start": v(64.36, 97.41) * mm, "end": v(60.72, 100.42) * mm});
            skLineSegment(sketch, "E308.MirrorCS", {"start": v(-48.6, 45.68) * mm, "end": v(-52.87, 45.06) * mm});
            skLineSegment(sketch, "E309.MirrorCS", {"start": v(-18.49, 71.25) * mm, "end": v(-13.87, 61.56) * mm});
            skLineSegment(sketch, "E310.MirrorCS", {"start": v(51.2, 48.65) * mm, "end": v(57.41, 55.3) * mm});
            skLineSegment(sketch, "E311.MirrorCS", {"start": v(76.66, 21.1) * mm, "end": v(85.91, 23.03) * mm});
            skLineSegment(sketch, "E312.MirrorCS", {"start": v(-12.99, 106.31) * mm, "end": v(-15.83, 107.43) * mm});
            skLineSegment(sketch, "E313.MirrorCS", {"start": v(85.91, 23.03) * mm, "end": v(83.46, 24.96) * mm});
            skLineSegment(sketch, "E314.MirrorCS", {"start": v(10.38, 81.2) * mm, "end": v(7.38, 79.41) * mm});
            skLineSegment(sketch, "E315.MirrorCS", {"start": v(79.88, 19.65) * mm, "end": v(76.66, 21.1) * mm});
            skLineSegment(sketch, "E316.MirrorCS", {"start": v(-9.48, 29.7) * mm, "end": v(-12.5, 31.05) * mm});
            skLineSegment(sketch, "E317.MirrorCS", {"start": v(62.36, 72.4) * mm, "end": v(68.98, 79.6) * mm});
            skLineSegment(sketch, "E318.MirrorCS", {"start": v(45.05, 40.27) * mm, "end": v(55.25, 47.14) * mm});
            skLineSegment(sketch, "E319.MirrorCS", {"start": v(-71.09, 105.54) * mm, "end": v(-79.22, 115.19) * mm});
            skLineSegment(sketch, "E320.MirrorCS", {"start": v(66.29, 80.47) * mm, "end": v(72.78, 85.67) * mm});
            skLineSegment(sketch, "E321.MirrorCS", {"start": v(54.9, 56.35) * mm, "end": v(60.34, 63.26) * mm});
            skLineSegment(sketch, "E322.MirrorCS", {"start": v(-47.96, 36.21) * mm, "end": v(-40.85, 31.02) * mm});
            skLineSegment(sketch, "E323.MirrorCS", {"start": v(80.39, 108.61) * mm, "end": v(88, 117.67) * mm});
            skLineSegment(sketch, "E324.MirrorCS", {"start": v(13.4, 72.2) * mm, "end": v(9.35, 71.69) * mm});
            skLineSegment(sketch, "E325.MirrorCS", {"start": v(57.01, 63.84) * mm, "end": v(65.36, 72.4) * mm});
            skLineSegment(sketch, "E326.MirrorCS", {"start": v(88, 117.67) * mm, "end": v(77.58, 110.01) * mm});
            skLineSegment(sketch, "E327.MirrorCS", {"start": v(-43.72, -1.39) * mm, "end": v(-45.42, -4.43) * mm});
            skLineSegment(sketch, "E328.MirrorCS", {"start": v(14.83, -8.82) * mm, "end": v(34.8, -5.46) * mm});
            skLineSegment(sketch, "E329.MirrorCS", {"start": v(116.24, 44.85) * mm, "end": v(105, 42.33) * mm});
            skLineSegment(sketch, "E330.MirrorCS", {"start": v(9.35, 71.69) * mm, "end": v(10.38, 81.2) * mm});
            skLineSegment(sketch, "E331.MirrorCS", {"start": v(-45.42, -4.43) * mm, "end": v(-30.27, -5.9) * mm});
            skLineSegment(sketch, "E332.MirrorCS", {"start": v(9.14, 59.7) * mm, "end": v(13.4, 72.2) * mm});
            skLineSegment(sketch, "E333.MirrorCS", {"start": v(7.38, 79.41) * mm, "end": v(7.99, 90.57) * mm});
            skLineSegment(sketch, "E334.MirrorCS", {"start": v(-8.78, 9.26) * mm, "end": v(-13.42, 28.95) * mm});
            skLineSegment(sketch, "E335.MirrorCS", {"start": v(31.05, -3.8) * mm, "end": v(44.67, -2.08) * mm});
            skLineSegment(sketch, "E336.MirrorCS", {"start": v(-53.06, 55.5) * mm, "end": v(-58.97, 54.9) * mm});
            skLineSegment(sketch, "E337.MirrorCS", {"start": v(34.8, -5.46) * mm, "end": v(31.05, -3.8) * mm});
            skLineSegment(sketch, "E338.MirrorCS", {"start": v(-79.22, 115.19) * mm, "end": v(-73.68, 103.44) * mm});
            skLineSegment(sketch, "E339.MirrorCS", {"start": v(-55.1, -1.14) * mm, "end": v(-43.72, -1.39) * mm});
            skLineSegment(sketch, "E340.MirrorCS", {"start": v(-58.97, 54.9) * mm, "end": v(-48.6, 45.68) * mm});
            skLineSegment(sketch, "E341.MirrorCS", {"start": v(37.07, 75.15) * mm, "end": v(34.27, 65.55) * mm});
            skLineSegment(sketch, "E342.MirrorCS", {"start": v(-6.3, -15.51) * mm, "end": v(-5.1, -31.65) * mm});
            skLineSegment(sketch, "E343.MirrorCS", {"start": v(-1.24, 144.46) * mm, "end": v(-1.4, 172.45) * mm});
            skLineSegment(sketch, "E344.MirrorCS", {"start": v(-1.4, 172.45) * mm, "end": v(-5.06, 145.09) * mm});
            skCircle(sketch, "E345", {"center": v(-1.6, -43.65) * mm, "radius": 7.5 * mm});
            skArc(sketch, "E346", {"start": v(-5.1, -31.65) * mm, "mid": v(-1.81, -56.15) * mm, "end": v(2.32, -31.78) * mm});
            skLineSegment(sketch, "E347", {"start": v(2.32, -31.78) * mm, "end": v(3.97, -16.71) * mm});
            skSolve(sketch);
        }
        {
            var Q0;
            Q0=qCreatedBy(id+"F0.planeOp",FACE);
            var sketch = newSketch(context, id + "F2", { "sketchPlane" : qUnion([Q0])});
            skLineSegment(sketch, "E348", {"start": v(-3.34, 5.11) * mm, "end": v(-3.34, 14.82) * mm});
            skLineSegment(sketch, "E349", {"start": v(-3.34, 14.82) * mm, "end": v(-9.6, 19.54) * mm});
            skLineSegment(sketch, "E350", {"start": v(-9.6, 19.54) * mm, "end": v(-3.57, 17) * mm});
            skLineSegment(sketch, "E351", {"start": v(-3.57, 17) * mm, "end": v(-3.57, 29.11) * mm});
            skLineSegment(sketch, "E352", {"start": v(-3.57, 29.11) * mm, "end": v(-9.6, 35.6) * mm});
            skLineSegment(sketch, "E353", {"start": v(-9.6, 35.6) * mm, "end": v(-4.41, 31.7) * mm});
            skLineSegment(sketch, "E354", {"start": v(-4.41, 31.7) * mm, "end": v(-4.41, 44.35) * mm});
            skLineSegment(sketch, "E355", {"start": v(-4.41, 44.35) * mm, "end": v(-11.7, 48.45) * mm});
            skLineSegment(sketch, "E356", {"start": v(-11.7, 48.45) * mm, "end": v(-4.63, 46.54) * mm});
            skLineSegment(sketch, "E357", {"start": v(-4.63, 46.54) * mm, "end": v(-4.63, 57.4) * mm});
            skLineSegment(sketch, "E358", {"start": v(-4.63, 57.4) * mm, "end": v(-10.97, 63.57) * mm});
            skLineSegment(sketch, "E359", {"start": v(-10.97, 63.57) * mm, "end": v(-4.75, 60.48) * mm});
            skLineSegment(sketch, "E360", {"start": v(-4.75, 60.48) * mm, "end": v(-5.6, 73.67) * mm});
            skLineSegment(sketch, "E361", {"start": v(-5.6, 73.67) * mm, "end": v(-10.98, 78.91) * mm});
            skLineSegment(sketch, "E362", {"start": v(-10.98, 78.91) * mm, "end": v(-5.85, 75.04) * mm});
            skLineSegment(sketch, "E363", {"start": v(-5.85, 75.04) * mm, "end": v(-6.95, 90.37) * mm});
            skLineSegment(sketch, "E364", {"start": v(-6.95, 90.37) * mm, "end": v(-12.08, 94.24) * mm});
            skLineSegment(sketch, "E365", {"start": v(-12.08, 94.24) * mm, "end": v(-7.04, 92.35) * mm});
            skLineSegment(sketch, "E366", {"start": v(-7.04, 92.35) * mm, "end": v(-7.04, 103.3) * mm});
            skLineSegment(sketch, "E367", {"start": v(-7.04, 103.3) * mm, "end": v(-10.69, 108.23) * mm});
            skLineSegment(sketch, "E368", {"start": v(-10.69, 108.23) * mm, "end": v(-7.43, 105.77) * mm});
            skLineSegment(sketch, "E369", {"start": v(-7.43, 105.77) * mm, "end": v(-7.04, 118.33) * mm});
            skLineSegment(sketch, "E370", {"start": v(-7.04, 118.33) * mm, "end": v(-9.45, 123.14) * mm});
            skLineSegment(sketch, "E371", {"start": v(-9.45, 123.14) * mm, "end": v(-7.04, 119.9) * mm});
            skLineSegment(sketch, "E372", {"start": v(-7.04, 119.9) * mm, "end": v(-4.3, 131.15) * mm});
            skLineSegment(sketch, "E373", {"start": v(-4.3, 131.15) * mm, "end": v(-7.04, 134.86) * mm});
            skLineSegment(sketch, "E374", {"start": v(-7.04, 134.86) * mm, "end": v(-4.3, 132.79) * mm});
            skLineSegment(sketch, "E375", {"start": v(-4.3, 132.79) * mm, "end": v(-3.4, 142.1) * mm});
            skLineSegment(sketch, "E376", {"start": v(-3.4, 142.1) * mm, "end": v(-3.77, 130.46) * mm});
            skLineSegment(sketch, "E377", {"start": v(-3.77, 130.46) * mm, "end": v(0.51, 133.2) * mm});
            skLineSegment(sketch, "E378", {"start": v(0.51, 133.2) * mm, "end": v(-3.94, 129.1) * mm});
            skLineSegment(sketch, "E379", {"start": v(-3.94, 129.1) * mm, "end": v(-5.65, 122.06) * mm});
            skLineSegment(sketch, "E380", {"start": v(-5.65, 122.06) * mm, "end": v(-1.34, 124.5) * mm});
            skLineSegment(sketch, "E381", {"start": v(-1.34, 124.5) * mm, "end": v(-5.88, 120.76) * mm});
            skLineSegment(sketch, "E382", {"start": v(-5.88, 120.76) * mm, "end": v(-6.3, 113.81) * mm});
            skLineSegment(sketch, "E383", {"start": v(-6.3, 113.81) * mm, "end": v(0.34, 116.39) * mm});
            skLineSegment(sketch, "E384", {"start": v(0.34, 116.39) * mm, "end": v(-6.1, 112.75) * mm});
            skLineSegment(sketch, "E385", {"start": v(-6.1, 112.75) * mm, "end": v(-5.35, 101.77) * mm});
            skLineSegment(sketch, "E386", {"start": v(-5.35, 101.77) * mm, "end": v(1.82, 106.15) * mm});
            skLineSegment(sketch, "E387", {"start": v(1.82, 106.15) * mm, "end": v(-5.31, 100.28) * mm});
            skLineSegment(sketch, "E388", {"start": v(-5.31, 100.28) * mm, "end": v(-4.8, 85.08) * mm});
            skLineSegment(sketch, "E389", {"start": v(-4.8, 85.08) * mm, "end": v(2.6, 88.15) * mm});
            skLineSegment(sketch, "E390", {"start": v(2.6, 88.15) * mm, "end": v(-4.3, 83.04) * mm});
            skLineSegment(sketch, "E391", {"start": v(-4.3, 83.04) * mm, "end": v(-3.66, 70.78) * mm});
            skLineSegment(sketch, "E392", {"start": v(-3.66, 70.78) * mm, "end": v(5.16, 76.08) * mm});
            skLineSegment(sketch, "E393", {"start": v(5.16, 76.08) * mm, "end": v(-3.43, 68.17) * mm});
            skLineSegment(sketch, "E394", {"start": v(-3.43, 68.17) * mm, "end": v(-2.87, 54.83) * mm});
            skLineSegment(sketch, "E395", {"start": v(-2.87, 54.83) * mm, "end": v(8.35, 57.95) * mm});
            skLineSegment(sketch, "E396", {"start": v(8.35, 57.95) * mm, "end": v(-2.73, 52.41) * mm});
            skLineSegment(sketch, "E397", {"start": v(-2.73, 52.41) * mm, "end": v(-2.5, 40.2) * mm});
            skLineSegment(sketch, "E398", {"start": v(-2.5, 40.2) * mm, "end": v(6.35, 44.8) * mm});
            skLineSegment(sketch, "E399", {"start": v(6.35, 44.8) * mm, "end": v(-2.45, 38.3) * mm});
            skLineSegment(sketch, "E400", {"start": v(-2.45, 38.3) * mm, "end": v(-1.9, 27.1) * mm});
            skLineSegment(sketch, "E401", {"start": v(-1.9, 27.1) * mm, "end": v(4.3, 30.17) * mm});
            skLineSegment(sketch, "E402", {"start": v(4.3, 30.17) * mm, "end": v(-1.82, 25.14) * mm});
            skLineSegment(sketch, "E403", {"start": v(-1.82, 25.14) * mm, "end": v(-1.6, 11.9) * mm});
            skLineSegment(sketch, "E404", {"start": v(-1.6, 11.9) * mm, "end": v(3.14, 14.57) * mm});
            skLineSegment(sketch, "E405", {"start": v(3.14, 14.57) * mm, "end": v(-1.66, 9.65) * mm});
            skLineSegment(sketch, "E406", {"start": v(-1.66, 9.65) * mm, "end": v(-1.58, 4.92) * mm});
            skLineSegment(sketch, "E407", {"start": v(-1.58, 4.92) * mm, "end": v(-3.34, 5.11) * mm});
            skLineSegment(sketch, "E408", {"start": v(-13.6, 3.91) * mm, "end": v(-20.7, 16.52) * mm});
            skLineSegment(sketch, "E409", {"start": v(-20.7, 16.52) * mm, "end": v(-29.51, 19.54) * mm});
            skLineSegment(sketch, "E410", {"start": v(-29.51, 19.54) * mm, "end": v(-21.56, 18.14) * mm});
            skLineSegment(sketch, "E411", {"start": v(-21.56, 18.14) * mm, "end": v(-32.3, 32.64) * mm});
            skLineSegment(sketch, "E412", {"start": v(-32.3, 32.64) * mm, "end": v(-40.72, 34.7) * mm});
            skLineSegment(sketch, "E413", {"start": v(-40.72, 34.7) * mm, "end": v(-33.4, 34.82) * mm});
            skLineSegment(sketch, "E414", {"start": v(-33.4, 34.82) * mm, "end": v(-43.24, 52.27) * mm});
            skLineSegment(sketch, "E415", {"start": v(-43.24, 52.27) * mm, "end": v(-49.85, 52.16) * mm});
            skLineSegment(sketch, "E416", {"start": v(-49.85, 52.16) * mm, "end": v(-43.97, 53.48) * mm});
            skLineSegment(sketch, "E417", {"start": v(-43.97, 53.48) * mm, "end": v(-53.77, 68.1) * mm});
            skLineSegment(sketch, "E418", {"start": v(-53.77, 68.1) * mm, "end": v(-60.34, 68) * mm});
            skLineSegment(sketch, "E419", {"start": v(-60.34, 68) * mm, "end": v(-54.63, 69.6) * mm});
            skLineSegment(sketch, "E420", {"start": v(-54.63, 69.6) * mm, "end": v(-61.41, 79.71) * mm});
            skLineSegment(sketch, "E421", {"start": v(-61.41, 79.71) * mm, "end": v(-66.08, 78.83) * mm});
            skLineSegment(sketch, "E422", {"start": v(-66.08, 78.83) * mm, "end": v(-62.02, 80.5) * mm});
            skLineSegment(sketch, "E423", {"start": v(-62.02, 80.5) * mm, "end": v(-64.84, 87.33) * mm});
            skLineSegment(sketch, "E424", {"start": v(-64.84, 87.33) * mm, "end": v(-68.93, 88.32) * mm});
            skLineSegment(sketch, "E425", {"start": v(-68.93, 88.32) * mm, "end": v(-65.27, 88.38) * mm});
            skLineSegment(sketch, "E426", {"start": v(-65.27, 88.38) * mm, "end": v(-69.54, 98.7) * mm});
            skLineSegment(sketch, "E427", {"start": v(-69.54, 98.7) * mm, "end": v(-65.95, 92.35) * mm});
            skLineSegment(sketch, "E428", {"start": v(-65.95, 92.35) * mm, "end": v(-63.37, 95) * mm});
            skLineSegment(sketch, "E429", {"start": v(-63.37, 95) * mm, "end": v(-65.2, 91.36) * mm});
            skLineSegment(sketch, "E430", {"start": v(-65.2, 91.36) * mm, "end": v(-62.45, 84.73) * mm});
            skLineSegment(sketch, "E431", {"start": v(-62.45, 84.73) * mm, "end": v(-59.77, 88.28) * mm});
            skLineSegment(sketch, "E432", {"start": v(-59.77, 88.28) * mm, "end": v(-61.66, 83.4) * mm});
            skLineSegment(sketch, "E433", {"start": v(-61.66, 83.4) * mm, "end": v(-56.47, 75.67) * mm});
            skLineSegment(sketch, "E434", {"start": v(-56.47, 75.67) * mm, "end": v(-53.43, 79.7) * mm});
            skLineSegment(sketch, "E435", {"start": v(-53.43, 79.7) * mm, "end": v(-55.59, 74.38) * mm});
            skLineSegment(sketch, "E436", {"start": v(-55.59, 74.38) * mm, "end": v(-49.27, 64.95) * mm});
            skLineSegment(sketch, "E437", {"start": v(-49.27, 64.95) * mm, "end": v(-46.77, 70.3) * mm});
            skLineSegment(sketch, "E438", {"start": v(-46.77, 70.3) * mm, "end": v(-48.45, 63.4) * mm});
            skLineSegment(sketch, "E439", {"start": v(-48.45, 63.4) * mm, "end": v(-37, 46.31) * mm});
            skLineSegment(sketch, "E440", {"start": v(-37, 46.31) * mm, "end": v(-33.14, 53.3) * mm});
            skLineSegment(sketch, "E441", {"start": v(-33.14, 53.3) * mm, "end": v(-35.37, 44.2) * mm});
            skLineSegment(sketch, "E442", {"start": v(-35.37, 44.2) * mm, "end": v(-27.57, 30.38) * mm});
            skLineSegment(sketch, "E443", {"start": v(-27.57, 30.38) * mm, "end": v(-25.03, 35.72) * mm});
            skLineSegment(sketch, "E444", {"start": v(-25.03, 35.72) * mm, "end": v(-26.07, 28.4) * mm});
            skLineSegment(sketch, "E445", {"start": v(-26.07, 28.4) * mm, "end": v(-18, 16.36) * mm});
            skLineSegment(sketch, "E446", {"start": v(-18, 16.36) * mm, "end": v(-15.6, 19.54) * mm});
            skLineSegment(sketch, "E447", {"start": v(-15.6, 19.54) * mm, "end": v(-16.8, 13.97) * mm});
            skLineSegment(sketch, "E448", {"start": v(-16.8, 13.97) * mm, "end": v(-11.68, 6.33) * mm});
            skLineSegment(sketch, "E449", {"start": v(-11.68, 6.33) * mm, "end": v(-13.6, 3.91) * mm});
            skLineSegment(sketch, "E450.MirrorCS", {"start": v(65.05, 91) * mm, "end": v(62, 84.5) * mm});
            skLineSegment(sketch, "E451.MirrorCS", {"start": v(64.51, 86.98) * mm, "end": v(68.64, 87.79) * mm});
            skLineSegment(sketch, "E452.MirrorCS", {"start": v(68.64, 87.79) * mm, "end": v(64.99, 88.02) * mm});
            skLineSegment(sketch, "E453.MirrorCS", {"start": v(14.47, 18.23) * mm, "end": v(12.21, 21.52) * mm});
            skLineSegment(sketch, "E454.MirrorCS", {"start": v(61.15, 83.2) * mm, "end": v(55.62, 75.72) * mm});
            skLineSegment(sketch, "E455.MirrorCS", {"start": v(59.13, 67.88) * mm, "end": v(53.5, 69.74) * mm});
            skLineSegment(sketch, "E456.MirrorCS", {"start": v(52.76, 79.89) * mm, "end": v(54.68, 74.47) * mm});
            skLineSegment(sketch, "E457.MirrorCS", {"start": v(62, 84.5) * mm, "end": v(59.49, 88.16) * mm});
            skLineSegment(sketch, "E458.MirrorCS", {"start": v(65.86, 91.95) * mm, "end": v(63.4, 94.72) * mm});
            skLineSegment(sketch, "E459.MirrorCS", {"start": v(60.74, 79.53) * mm, "end": v(65.36, 78.44) * mm});
            skLineSegment(sketch, "E460.MirrorCS", {"start": v(61.38, 80.3) * mm, "end": v(64.51, 86.98) * mm});
            skLineSegment(sketch, "E461.MirrorCS", {"start": v(47.93, 65.34) * mm, "end": v(45.68, 70.8) * mm});
            skLineSegment(sketch, "E462.MirrorCS", {"start": v(59.49, 88.16) * mm, "end": v(61.15, 83.2) * mm});
            skLineSegment(sketch, "E463.MirrorCS", {"start": v(64.99, 88.02) * mm, "end": v(69.73, 98.13) * mm});
            skLineSegment(sketch, "E464.MirrorCS", {"start": v(63.4, 94.72) * mm, "end": v(65.05, 91) * mm});
            skLineSegment(sketch, "E465.MirrorCS", {"start": v(34.82, 47.29) * mm, "end": v(31.3, 54.45) * mm});
            skLineSegment(sketch, "E466.MirrorCS", {"start": v(54.68, 74.47) * mm, "end": v(47.93, 65.34) * mm});
            skLineSegment(sketch, "E467.MirrorCS", {"start": v(55.62, 75.72) * mm, "end": v(52.76, 79.89) * mm});
            skLineSegment(sketch, "E468.MirrorCS", {"start": v(29.5, 33.85) * mm, "end": v(38, 35.51) * mm});
            skLineSegment(sketch, "E469.MirrorCS", {"start": v(24.67, 31.8) * mm, "end": v(22.38, 37.25) * mm});
            skLineSegment(sketch, "E470.MirrorCS", {"start": v(17.18, 18.26) * mm, "end": v(26.12, 20.88) * mm});
            skLineSegment(sketch, "E471.MirrorCS", {"start": v(45.68, 70.8) * mm, "end": v(47.05, 63.83) * mm});
            skLineSegment(sketch, "E472.MirrorCS", {"start": v(41.33, 52.95) * mm, "end": v(47.93, 52.54) * mm});
            skLineSegment(sketch, "E473.MirrorCS", {"start": v(22.38, 37.25) * mm, "end": v(23.08, 29.9) * mm});
            skLineSegment(sketch, "E474.MirrorCS", {"start": v(65.36, 78.44) * mm, "end": v(61.38, 80.3) * mm});
            skLineSegment(sketch, "E475.MirrorCS", {"start": v(52.58, 68.29) * mm, "end": v(59.13, 67.88) * mm});
            skLineSegment(sketch, "E476.MirrorCS", {"start": v(26.12, 20.88) * mm, "end": v(18.1, 19.85) * mm});
            skLineSegment(sketch, "E477.MirrorCS", {"start": v(31.3, 54.45) * mm, "end": v(33.1, 45.25) * mm});
            skLineSegment(sketch, "E478.MirrorCS", {"start": v(38, 35.51) * mm, "end": v(30.7, 35.97) * mm});
            skLineSegment(sketch, "E479.MirrorCS", {"start": v(53.5, 69.74) * mm, "end": v(60.74, 79.53) * mm});
            skLineSegment(sketch, "E480.MirrorCS", {"start": v(69.73, 98.13) * mm, "end": v(65.86, 91.95) * mm});
            skLineSegment(sketch, "E481.MirrorCS", {"start": v(47.93, 52.54) * mm, "end": v(42.12, 54.13) * mm});
            skLineSegment(sketch, "E482.MirrorCS", {"start": v(12.21, 21.52) * mm, "end": v(13.16, 15.9) * mm});
            skLineSegment(sketch, "E483.MirrorCS", {"start": v(18.1, 19.85) * mm, "end": v(29.5, 33.85) * mm});
            skLineSegment(sketch, "E484.MirrorCS", {"start": v(47.05, 63.83) * mm, "end": v(34.82, 47.29) * mm});
            skLineSegment(sketch, "E485.MirrorCS", {"start": v(23.08, 29.9) * mm, "end": v(14.47, 18.23) * mm});
            skLineSegment(sketch, "E486.MirrorCS", {"start": v(30.7, 35.97) * mm, "end": v(41.33, 52.95) * mm});
            skLineSegment(sketch, "E487.MirrorCS", {"start": v(42.12, 54.13) * mm, "end": v(52.58, 68.29) * mm});
            skLineSegment(sketch, "E488.MirrorCS", {"start": v(33.1, 45.25) * mm, "end": v(24.67, 31.8) * mm});
            skLineSegment(sketch, "E489", {"start": v(17.18, 18.26) * mm, "end": v(8.47, 1.9) * mm});
            skLineSegment(sketch, "E490", {"start": v(8.47, 1.9) * mm, "end": v(6.5, 2.95) * mm});
            skLineSegment(sketch, "E491", {"start": v(6.5, 2.95) * mm, "end": v(13.16, 15.9) * mm});
            skLineSegment(sketch, "E492", {"start": v(31.48, 3.96) * mm, "end": v(33.33, 11.24) * mm});
            skLineSegment(sketch, "E493", {"start": v(33.33, 11.24) * mm, "end": v(32.54, 4.85) * mm});
            skLineSegment(sketch, "E494", {"start": v(32.54, 4.85) * mm, "end": v(45.27, 13.48) * mm});
            skLineSegment(sketch, "E495", {"start": v(45.27, 13.48) * mm, "end": v(46.06, 19.86) * mm});
            skLineSegment(sketch, "E496", {"start": v(46.06, 19.86) * mm, "end": v(46.94, 14.55) * mm});
            skLineSegment(sketch, "E497", {"start": v(46.94, 14.55) * mm, "end": v(56.42, 20.02) * mm});
            skLineSegment(sketch, "E498", {"start": v(56.42, 20.02) * mm, "end": v(58.86, 25.64) * mm});
            skLineSegment(sketch, "E499", {"start": v(58.86, 25.64) * mm, "end": v(58.36, 21.59) * mm});
            skLineSegment(sketch, "E500", {"start": v(58.36, 21.59) * mm, "end": v(69.43, 27.53) * mm});
            skLineSegment(sketch, "E501", {"start": v(69.43, 27.53) * mm, "end": v(72.4, 32.02) * mm});
            skLineSegment(sketch, "E502", {"start": v(72.4, 32.02) * mm, "end": v(70.79, 28.32) * mm});
            skLineSegment(sketch, "E503", {"start": v(70.79, 28.32) * mm, "end": v(81.91, 31.57) * mm});
            skLineSegment(sketch, "E504", {"start": v(81.91, 31.57) * mm, "end": v(83.75, 35.8) * mm});
            skLineSegment(sketch, "E505", {"start": v(83.75, 35.8) * mm, "end": v(83.33, 32.39) * mm});
            skLineSegment(sketch, "E506", {"start": v(83.33, 32.39) * mm, "end": v(91.84, 36.26) * mm});
            skLineSegment(sketch, "E507", {"start": v(91.84, 36.26) * mm, "end": v(81.57, 30.77) * mm});
            skLineSegment(sketch, "E508", {"start": v(81.57, 30.77) * mm, "end": v(86.09, 28.43) * mm});
            skLineSegment(sketch, "E509", {"start": v(86.09, 28.43) * mm, "end": v(80.31, 30.23) * mm});
            skLineSegment(sketch, "E510", {"start": v(80.31, 30.23) * mm, "end": v(73.36, 28.2) * mm});
            skLineSegment(sketch, "E511", {"start": v(73.36, 28.2) * mm, "end": v(77.62, 25.67) * mm});
            skLineSegment(sketch, "E512", {"start": v(77.62, 25.67) * mm, "end": v(72.12, 27.74) * mm});
            skLineSegment(sketch, "E513", {"start": v(72.12, 27.74) * mm, "end": v(65.9, 24.63) * mm});
            skLineSegment(sketch, "E514", {"start": v(65.9, 24.63) * mm, "end": v(71.45, 20.17) * mm});
            skLineSegment(sketch, "E515", {"start": v(71.45, 20.17) * mm, "end": v(65.07, 23.93) * mm});
            skLineSegment(sketch, "E516", {"start": v(65.07, 23.93) * mm, "end": v(55.94, 17.8) * mm});
            skLineSegment(sketch, "E517", {"start": v(55.94, 17.8) * mm, "end": v(63.32, 13.76) * mm});
            skLineSegment(sketch, "E518", {"start": v(63.32, 13.76) * mm, "end": v(54.67, 17.01) * mm});
            skLineSegment(sketch, "E519", {"start": v(54.67, 17.01) * mm, "end": v(41.76, 8.98) * mm});
            skLineSegment(sketch, "E520", {"start": v(41.76, 8.98) * mm, "end": v(48.12, 4.1) * mm});
            skLineSegment(sketch, "E521", {"start": v(48.12, 4.1) * mm, "end": v(40.25, 7.51) * mm});
            skLineSegment(sketch, "E522", {"start": v(40.25, 7.51) * mm, "end": v(29.95, 0.83) * mm});
            skLineSegment(sketch, "E523.0", {"start": v(57.64, 22.83) * mm, "end": v(58.36, 21.59) * mm, "construction": true});
            skLineSegment(sketch, "E524", {"start": v(31.48, 3.96) * mm, "end": v(15.61, -2.73) * mm});
            skLineSegment(sketch, "E525", {"start": v(15.61, -2.73) * mm, "end": v(16.85, -4.64) * mm});
            skLineSegment(sketch, "E526", {"start": v(16.85, -4.64) * mm, "end": v(29.95, 0.83) * mm});
            skLineSegment(sketch, "E527.MirrorCS", {"start": v(-69.58, 25.23) * mm, "end": v(-67.65, 21.68) * mm});
            skLineSegment(sketch, "E528.MirrorCS", {"start": v(-81.21, 28) * mm, "end": v(-80.5, 24.64) * mm});
            skLineSegment(sketch, "E529.MirrorCS", {"start": v(-77.3, 22.76) * mm, "end": v(-70.2, 21.34) * mm});
            skLineSegment(sketch, "E530.MirrorCS", {"start": v(-74.23, 18.46) * mm, "end": v(-68.93, 21) * mm});
            skLineSegment(sketch, "E531.MirrorCS", {"start": v(-66.23, 21.02) * mm, "end": v(-69.58, 25.23) * mm});
            skLineSegment(sketch, "E532.MirrorCS", {"start": v(-79.01, 23.95) * mm, "end": v(-81.21, 28) * mm});
            skLineSegment(sketch, "E533.MirrorCS", {"start": v(-67.65, 21.68) * mm, "end": v(-79.01, 23.95) * mm});
            skLineSegment(sketch, "E534.MirrorCS", {"start": v(-70.2, 21.34) * mm, "end": v(-74.23, 18.46) * mm});
            skLineSegment(sketch, "E535.MirrorCS", {"start": v(-42.27, 15.41) * mm, "end": v(-42.69, 10.04) * mm});
            skLineSegment(sketch, "E536.MirrorCS", {"start": v(-28.84, 7.93) * mm, "end": v(-27.5, 1.64) * mm});
            skLineSegment(sketch, "E537.MirrorCS", {"start": v(-54.08, 17.36) * mm, "end": v(-54.68, 16.06) * mm, "construction": true});
            skLineSegment(sketch, "E538.MirrorCS", {"start": v(-82.9, 20.46) * mm, "end": v(-77.3, 22.76) * mm});
            skLineSegment(sketch, "E539.MirrorCS", {"start": v(-55.54, 20.06) * mm, "end": v(-54.68, 16.06) * mm});
            skLineSegment(sketch, "E540.MirrorCS", {"start": v(-52.61, 14.67) * mm, "end": v(-55.54, 20.06) * mm});
            skLineSegment(sketch, "E541.MirrorCS", {"start": v(-62.46, 18.43) * mm, "end": v(-67.6, 13.5) * mm});
            skLineSegment(sketch, "E542.MirrorCS", {"start": v(-58.94, 7.84) * mm, "end": v(-50.6, 11.83) * mm});
            skLineSegment(sketch, "E543.MirrorCS", {"start": v(-54.68, 16.06) * mm, "end": v(-66.23, 21.02) * mm});
            skLineSegment(sketch, "E544.MirrorCS", {"start": v(-9.98, -4.44) * mm, "end": v(-11.04, -6.45) * mm});
            skLineSegment(sketch, "E545.MirrorCS", {"start": v(-26.37, 0.84) * mm, "end": v(-28.84, 7.93) * mm});
            skLineSegment(sketch, "E546.MirrorCS", {"start": v(-80.5, 24.64) * mm, "end": v(-89.32, 27.76) * mm});
            skLineSegment(sketch, "E547.MirrorCS", {"start": v(-42.96, -0.47) * mm, "end": v(-35.41, 3.62) * mm});
            skLineSegment(sketch, "E548.MirrorCS", {"start": v(-89.32, 27.76) * mm, "end": v(-78.6, 23.19) * mm});
            skLineSegment(sketch, "E549.MirrorCS", {"start": v(-51.94, 12.5) * mm, "end": v(-58.94, 7.84) * mm});
            skLineSegment(sketch, "E550.MirrorCS", {"start": v(-78.6, 23.19) * mm, "end": v(-82.9, 20.46) * mm});
            skLineSegment(sketch, "E551.MirrorCS", {"start": v(-61.57, 17.81) * mm, "end": v(-51.94, 12.5) * mm});
            skLineSegment(sketch, "E552.MirrorCS", {"start": v(-27.5, 1.64) * mm, "end": v(-40.93, 9.12) * mm});
            skLineSegment(sketch, "E553.MirrorCS", {"start": v(-68.93, 21) * mm, "end": v(-62.46, 18.43) * mm});
            skLineSegment(sketch, "E554.MirrorCS", {"start": v(-37.05, 4.95) * mm, "end": v(-42.96, -0.47) * mm});
            skLineSegment(sketch, "E555.MirrorCS", {"start": v(-50.6, 11.83) * mm, "end": v(-37.05, 4.95) * mm});
            skLineSegment(sketch, "E556.MirrorCS", {"start": v(-67.6, 13.5) * mm, "end": v(-61.57, 17.81) * mm});
            skLineSegment(sketch, "E557.MirrorCS", {"start": v(-42.69, 10.04) * mm, "end": v(-52.61, 14.67) * mm});
            skLineSegment(sketch, "E558.MirrorCS", {"start": v(-35.41, 3.62) * mm, "end": v(-24.57, -2.14) * mm});
            skLineSegment(sketch, "E559.MirrorCS", {"start": v(-40.93, 9.12) * mm, "end": v(-42.27, 15.41) * mm});
            skLineSegment(sketch, "E560.MirrorCS", {"start": v(-26.37, 0.84) * mm, "end": v(-9.98, -4.44) * mm});
            skLineSegment(sketch, "E561.MirrorCS", {"start": v(-11.04, -6.45) * mm, "end": v(-24.57, -2.14) * mm});
            skSolve(sketch);
        }
        {
            var Q0;
            Q0=makeQuery(id+"F1.imprint","IMPRINT",FACE,{"disambiguationData":[TD([[makeQuery(id+"F1.imprint","IMPRINT",EDGE,{"derivedFrom":sQuery(id+"F1.wireOp",EDGE,"E0.MirrorCS")}),1.0]])]});
            extrude(context, id + "F3", {"entities" : qUnion([Q0]), "depth" : 2.5 * mm, "offsetDistance" : 25 * mm});
        }
        {
            var Q0;
            Q0=makeQuery(id+"F2.imprint","IMPRINT",FACE,{"disambiguationData":[TD([[makeQuery(id+"F2.imprint","IMPRINT",EDGE,{"derivedFrom":sQuery(id+"F2.wireOp",EDGE,"E527.MirrorCS")}),1.0]])]});
            var Q1;
            Q1=makeQuery(id+"F2.imprint","IMPRINT",FACE,{"disambiguationData":[TD([[makeQuery(id+"F2.imprint","IMPRINT",EDGE,{"derivedFrom":sQuery(id+"F2.wireOp",EDGE,"E408")}),-1.0]])]});
            var Q2;
            Q2=makeQuery(id+"F2.imprint","IMPRINT",FACE,{"disambiguationData":[TD([[makeQuery(id+"F2.imprint","IMPRINT",EDGE,{"derivedFrom":sQuery(id+"F2.wireOp",EDGE,"E348")}),-1.0]])]});
            var Q3;
            Q3=makeQuery(id+"F2.imprint","IMPRINT",FACE,{"disambiguationData":[TD([[makeQuery(id+"F2.imprint","IMPRINT",EDGE,{"derivedFrom":sQuery(id+"F2.wireOp",EDGE,"E450.MirrorCS")}),1.0]])]});
            var Q4;
            Q4=makeQuery(id+"F2.imprint","IMPRINT",FACE,{"disambiguationData":[TD([[makeQuery(id+"F2.imprint","IMPRINT",EDGE,{"derivedFrom":sQuery(id+"F2.wireOp",EDGE,"E492")}),-1.0]])]});
            extrude(context, id + "F4", {"entities" : qUnion([Q0, Q1, Q2, Q3, Q4]), "operationType" : NewBodyOperationType.ADD, "depth" : 0.6 * mm, "offsetDistance" : 25 * mm});
        }
        {
            var Q0;
            Q0=makeQuery(id+"F4.opExtrude","CAP_EDGE",EDGE,{"disambiguationData":[OSD([sQuery(id+"F2.wireOp",EDGE,"E544.MirrorCS")])],"isStart":false});
            var Q1;
            Q1=makeQuery(id+"F4.opExtrude","CAP_EDGE",EDGE,{"disambiguationData":[OSD([sQuery(id+"F2.wireOp",EDGE,"E449")])],"isStart":false});
            var Q2;
            Q2=makeQuery(id+"F4.opExtrude","CAP_EDGE",EDGE,{"disambiguationData":[OSD([sQuery(id+"F2.wireOp",EDGE,"E407")])],"isStart":false});
            var Q3;
            Q3=makeQuery(id+"F4.opExtrude","CAP_EDGE",EDGE,{"disambiguationData":[OSD([sQuery(id+"F2.wireOp",EDGE,"E490")])],"isStart":false});
            var Q4;
            Q4=makeQuery(id+"F4.opExtrude","CAP_EDGE",EDGE,{"disambiguationData":[OSD([sQuery(id+"F2.wireOp",EDGE,"E525")])],"isStart":false});
            var Q5;
            Q5=makeQuery(id+"F3.opExtrude","SWEPT_EDGE",EDGE,{"disambiguationData":[OSD([sQuery(id+"F1.wireOp",EDGE,"E342.MirrorCS"),sQuery(id+"F1.wireOp",EDGE,"E346")])]});
            var Q6;
            Q6=makeQuery(id+"F3.opExtrude","SWEPT_EDGE",EDGE,{"disambiguationData":[OSD([sQuery(id+"F1.wireOp",EDGE,"E346"),sQuery(id+"F1.wireOp",EDGE,"E347")])]});
            fillet(context, id + "F5", {"entities" : qUnion([Q0, Q1, Q2, Q3, Q4, Q5, Q6]), "tangentPropagation" : true, "radius" : 15 * mm, "defaultsChanged" : false, "vertexSettings" : [], "allowEdgeOverflow" : false});
        }
        {
            var Q0;
            Q0=makeQuery(id+"F3.opExtrude","CAP_EDGE",EDGE,{"disambiguationData":[OSD([sQuery(id+"F1.wireOp",EDGE,"E331.MirrorCS")])],"isStart":false});
            var Q1;
            Q1=makeQuery(id+"F3.opExtrude","CAP_EDGE",EDGE,{"disambiguationData":[OSD([sQuery(id+"F1.wireOp",EDGE,"E211.MirrorCS")])],"isStart":false});
            var Q2;
            Q2=makeQuery(id+"F3.opExtrude","CAP_EDGE",EDGE,{"disambiguationData":[OSD([sQuery(id+"F1.wireOp",EDGE,"E160.MirrorCS")])],"isStart":false});
            var Q3;
            Q3=makeQuery(id+"F3.opExtrude","CAP_EDGE",EDGE,{"disambiguationData":[OSD([sQuery(id+"F1.wireOp",EDGE,"E192.MirrorCS")])],"isStart":false});
            var Q4;
            Q4=makeQuery(id+"F3.opExtrude","CAP_EDGE",EDGE,{"disambiguationData":[OSD([sQuery(id+"F1.wireOp",EDGE,"E141.MirrorCS")])],"isStart":false});
            var Q5;
            Q5=makeQuery(id+"F3.opExtrude","CAP_EDGE",EDGE,{"disambiguationData":[OSD([sQuery(id+"F1.wireOp",EDGE,"E195.MirrorCS")])],"isStart":false});
            var Q6;
            Q6=makeQuery(id+"F3.opExtrude","CAP_EDGE",EDGE,{"disambiguationData":[OSD([sQuery(id+"F1.wireOp",EDGE,"E242.MirrorCS")])],"isStart":false});
            var Q7;
            Q7=makeQuery(id+"F3.opExtrude","CAP_EDGE",EDGE,{"disambiguationData":[OSD([sQuery(id+"F1.wireOp",EDGE,"E66.MirrorCS")])],"isStart":false});
            var Q8;
            Q8=makeQuery(id+"F3.opExtrude","CAP_EDGE",EDGE,{"disambiguationData":[OSD([sQuery(id+"F1.wireOp",EDGE,"E68.MirrorCS")])],"isStart":false});
            var Q9;
            Q9=makeQuery(id+"F3.opExtrude","CAP_EDGE",EDGE,{"disambiguationData":[OSD([sQuery(id+"F1.wireOp",EDGE,"E186.MirrorCS")])],"isStart":false});
            var Q10;
            Q10=makeQuery(id+"F3.opExtrude","CAP_EDGE",EDGE,{"disambiguationData":[OSD([sQuery(id+"F1.wireOp",EDGE,"E102.MirrorCS")])],"isStart":false});
            var Q11;
            Q11=makeQuery(id+"F3.opExtrude","CAP_EDGE",EDGE,{"disambiguationData":[OSD([sQuery(id+"F1.wireOp",EDGE,"E73.MirrorCS")])],"isStart":false});
            var Q12;
            Q12=makeQuery(id+"F3.opExtrude","CAP_EDGE",EDGE,{"disambiguationData":[OSD([sQuery(id+"F1.wireOp",EDGE,"E241.MirrorCS")])],"isStart":false});
            var Q13;
            Q13=makeQuery(id+"F3.opExtrude","CAP_EDGE",EDGE,{"disambiguationData":[OSD([sQuery(id+"F1.wireOp",EDGE,"E322.MirrorCS")])],"isStart":false});
            var Q14;
            Q14=makeQuery(id+"F3.opExtrude","CAP_EDGE",EDGE,{"disambiguationData":[OSD([sQuery(id+"F1.wireOp",EDGE,"E340.MirrorCS")])],"isStart":false});
            var Q15;
            Q15=makeQuery(id+"F3.opExtrude","CAP_EDGE",EDGE,{"disambiguationData":[OSD([sQuery(id+"F1.wireOp",EDGE,"E264.MirrorCS")])],"isStart":false});
            var Q16;
            Q16=makeQuery(id+"F3.opExtrude","CAP_EDGE",EDGE,{"disambiguationData":[OSD([sQuery(id+"F1.wireOp",EDGE,"E76.MirrorCS")])],"isStart":false});
            var Q17;
            Q17=makeQuery(id+"F3.opExtrude","CAP_EDGE",EDGE,{"disambiguationData":[OSD([sQuery(id+"F1.wireOp",EDGE,"E74.MirrorCS")])],"isStart":false});
            var Q18;
            Q18=makeQuery(id+"F3.opExtrude","CAP_EDGE",EDGE,{"disambiguationData":[OSD([sQuery(id+"F1.wireOp",EDGE,"E71.MirrorCS")])],"isStart":false});
            var Q19;
            Q19=makeQuery(id+"F3.opExtrude","CAP_EDGE",EDGE,{"disambiguationData":[OSD([sQuery(id+"F1.wireOp",EDGE,"E286.MirrorCS")])],"isStart":false});
            var Q20;
            Q20=makeQuery(id+"F3.opExtrude","CAP_EDGE",EDGE,{"disambiguationData":[OSD([sQuery(id+"F1.wireOp",EDGE,"E306.MirrorCS")])],"isStart":false});
            var Q21;
            Q21=makeQuery(id+"F3.opExtrude","CAP_EDGE",EDGE,{"disambiguationData":[OSD([sQuery(id+"F1.wireOp",EDGE,"E244.MirrorCS")])],"isStart":false});
            var Q22;
            Q22=makeQuery(id+"F3.opExtrude","CAP_EDGE",EDGE,{"disambiguationData":[OSD([sQuery(id+"F1.wireOp",EDGE,"E98.MirrorCS")])],"isStart":false});
            var Q23;
            Q23=makeQuery(id+"F3.opExtrude","CAP_EDGE",EDGE,{"disambiguationData":[OSD([sQuery(id+"F1.wireOp",EDGE,"E83.MirrorCS")])],"isStart":false});
            var Q24;
            Q24=makeQuery(id+"F3.opExtrude","CAP_EDGE",EDGE,{"disambiguationData":[OSD([sQuery(id+"F1.wireOp",EDGE,"E53.MirrorCS")])],"isStart":false});
            var Q25;
            Q25=makeQuery(id+"F3.opExtrude","CAP_EDGE",EDGE,{"disambiguationData":[OSD([sQuery(id+"F1.wireOp",EDGE,"E84.MirrorCS")])],"isStart":false});
            var Q26;
            Q26=makeQuery(id+"F3.opExtrude","CAP_EDGE",EDGE,{"disambiguationData":[OSD([sQuery(id+"F1.wireOp",EDGE,"E54.MirrorCS")])],"isStart":false});
            var Q27;
            Q27=makeQuery(id+"F3.opExtrude","CAP_EDGE",EDGE,{"disambiguationData":[OSD([sQuery(id+"F1.wireOp",EDGE,"E319.MirrorCS")])],"isStart":false});
            var Q28;
            Q28=makeQuery(id+"F3.opExtrude","CAP_EDGE",EDGE,{"disambiguationData":[OSD([sQuery(id+"F1.wireOp",EDGE,"E240.MirrorCS")])],"isStart":false});
            var Q29;
            Q29=makeQuery(id+"F3.opExtrude","CAP_EDGE",EDGE,{"disambiguationData":[OSD([sQuery(id+"F1.wireOp",EDGE,"E287.MirrorCS")])],"isStart":false});
            var Q30;
            Q30=makeQuery(id+"F3.opExtrude","CAP_EDGE",EDGE,{"disambiguationData":[OSD([sQuery(id+"F1.wireOp",EDGE,"E248.MirrorCS")])],"isStart":false});
            var Q31;
            Q31=makeQuery(id+"F3.opExtrude","CAP_EDGE",EDGE,{"disambiguationData":[OSD([sQuery(id+"F1.wireOp",EDGE,"E265.MirrorCS")])],"isStart":false});
            var Q32;
            Q32=makeQuery(id+"F3.opExtrude","CAP_EDGE",EDGE,{"disambiguationData":[OSD([sQuery(id+"F1.wireOp",EDGE,"E297.MirrorCS")])],"isStart":false});
            var Q33;
            Q33=makeQuery(id+"F3.opExtrude","CAP_EDGE",EDGE,{"disambiguationData":[OSD([sQuery(id+"F1.wireOp",EDGE,"E52.MirrorCS")])],"isStart":false});
            var Q34;
            Q34=makeQuery(id+"F3.opExtrude","CAP_EDGE",EDGE,{"disambiguationData":[OSD([sQuery(id+"F1.wireOp",EDGE,"E70.MirrorCS")])],"isStart":false});
            var Q35;
            Q35=makeQuery(id+"F3.opExtrude","CAP_EDGE",EDGE,{"disambiguationData":[OSD([sQuery(id+"F1.wireOp",EDGE,"E344.MirrorCS")])],"isStart":false});
            var Q36;
            Q36=makeQuery(id+"F3.opExtrude","CAP_EDGE",EDGE,{"disambiguationData":[OSD([sQuery(id+"F1.wireOp",EDGE,"E237.MirrorCS")])],"isStart":false});
            var Q37;
            Q37=makeQuery(id+"F3.opExtrude","CAP_EDGE",EDGE,{"disambiguationData":[OSD([sQuery(id+"F1.wireOp",EDGE,"E210.MirrorCS")])],"isStart":false});
            var Q38;
            Q38=makeQuery(id+"F3.opExtrude","CAP_EDGE",EDGE,{"disambiguationData":[OSD([sQuery(id+"F1.wireOp",EDGE,"E332.MirrorCS")])],"isStart":false});
            var Q39;
            Q39=makeQuery(id+"F3.opExtrude","CAP_EDGE",EDGE,{"disambiguationData":[OSD([sQuery(id+"F1.wireOp",EDGE,"E333.MirrorCS")])],"isStart":false});
            var Q40;
            Q40=makeQuery(id+"F3.opExtrude","CAP_EDGE",EDGE,{"disambiguationData":[OSD([sQuery(id+"F1.wireOp",EDGE,"E224.MirrorCS")])],"isStart":false});
            var Q41;
            Q41=makeQuery(id+"F3.opExtrude","CAP_EDGE",EDGE,{"disambiguationData":[OSD([sQuery(id+"F1.wireOp",EDGE,"E154.MirrorCS")])],"isStart":false});
            var Q42;
            Q42=makeQuery(id+"F3.opExtrude","CAP_EDGE",EDGE,{"disambiguationData":[OSD([sQuery(id+"F1.wireOp",EDGE,"E222.MirrorCS")])],"isStart":false});
            var Q43;
            Q43=makeQuery(id+"F3.opExtrude","CAP_EDGE",EDGE,{"disambiguationData":[OSD([sQuery(id+"F1.wireOp",EDGE,"E266.MirrorCS")])],"isStart":false});
            var Q44;
            Q44=makeQuery(id+"F3.opExtrude","CAP_EDGE",EDGE,{"disambiguationData":[OSD([sQuery(id+"F1.wireOp",EDGE,"E149.MirrorCS")])],"isStart":false});
            var Q45;
            Q45=makeQuery(id+"F3.opExtrude","CAP_EDGE",EDGE,{"disambiguationData":[OSD([sQuery(id+"F1.wireOp",EDGE,"E268.MirrorCS")])],"isStart":false});
            var Q46;
            Q46=makeQuery(id+"F3.opExtrude","CAP_EDGE",EDGE,{"disambiguationData":[OSD([sQuery(id+"F1.wireOp",EDGE,"E341.MirrorCS")])],"isStart":false});
            var Q47;
            Q47=makeQuery(id+"F3.opExtrude","CAP_EDGE",EDGE,{"disambiguationData":[OSD([sQuery(id+"F1.wireOp",EDGE,"E214.MirrorCS")])],"isStart":false});
            var Q48;
            Q48=makeQuery(id+"F3.opExtrude","CAP_EDGE",EDGE,{"disambiguationData":[OSD([sQuery(id+"F1.wireOp",EDGE,"E229.MirrorCS")])],"isStart":false});
            var Q49;
            Q49=makeQuery(id+"F3.opExtrude","CAP_EDGE",EDGE,{"disambiguationData":[OSD([sQuery(id+"F1.wireOp",EDGE,"E220.MirrorCS")])],"isStart":false});
            var Q50;
            Q50=makeQuery(id+"F3.opExtrude","CAP_EDGE",EDGE,{"disambiguationData":[OSD([sQuery(id+"F1.wireOp",EDGE,"E250.MirrorCS")])],"isStart":false});
            var Q51;
            Q51=makeQuery(id+"F3.opExtrude","CAP_EDGE",EDGE,{"disambiguationData":[OSD([sQuery(id+"F1.wireOp",EDGE,"E153.MirrorCS")])],"isStart":false});
            var Q52;
            Q52=makeQuery(id+"F3.opExtrude","CAP_EDGE",EDGE,{"disambiguationData":[OSD([sQuery(id+"F1.wireOp",EDGE,"E204.MirrorCS")])],"isStart":false});
            var Q53;
            Q53=makeQuery(id+"F3.opExtrude","CAP_EDGE",EDGE,{"disambiguationData":[OSD([sQuery(id+"F1.wireOp",EDGE,"E318.MirrorCS")])],"isStart":false});
            var Q54;
            Q54=makeQuery(id+"F3.opExtrude","CAP_EDGE",EDGE,{"disambiguationData":[OSD([sQuery(id+"F1.wireOp",EDGE,"E321.MirrorCS")])],"isStart":false});
            var Q55;
            Q55=makeQuery(id+"F3.opExtrude","CAP_EDGE",EDGE,{"disambiguationData":[OSD([sQuery(id+"F1.wireOp",EDGE,"E317.MirrorCS")])],"isStart":false});
            var Q56;
            Q56=makeQuery(id+"F3.opExtrude","CAP_EDGE",EDGE,{"disambiguationData":[OSD([sQuery(id+"F1.wireOp",EDGE,"E301.MirrorCS")])],"isStart":false});
            var Q57;
            Q57=makeQuery(id+"F3.opExtrude","CAP_EDGE",EDGE,{"disambiguationData":[OSD([sQuery(id+"F1.wireOp",EDGE,"E267.MirrorCS")])],"isStart":false});
            var Q58;
            Q58=makeQuery(id+"F3.opExtrude","CAP_EDGE",EDGE,{"disambiguationData":[OSD([sQuery(id+"F1.wireOp",EDGE,"E109.MirrorCS")])],"isStart":false});
            var Q59;
            Q59=makeQuery(id+"F3.opExtrude","CAP_EDGE",EDGE,{"disambiguationData":[OSD([sQuery(id+"F1.wireOp",EDGE,"E44.MirrorCS")])],"isStart":false});
            var Q60;
            Q60=makeQuery(id+"F3.opExtrude","CAP_EDGE",EDGE,{"disambiguationData":[OSD([sQuery(id+"F1.wireOp",EDGE,"E64.MirrorCS")])],"isStart":false});
            var Q61;
            Q61=makeQuery(id+"F3.opExtrude","CAP_EDGE",EDGE,{"disambiguationData":[OSD([sQuery(id+"F1.wireOp",EDGE,"E126.MirrorCS")])],"isStart":false});
            var Q62;
            Q62=makeQuery(id+"F3.opExtrude","CAP_EDGE",EDGE,{"disambiguationData":[OSD([sQuery(id+"F1.wireOp",EDGE,"E187.MirrorCS")])],"isStart":false});
            var Q63;
            Q63=makeQuery(id+"F3.opExtrude","CAP_EDGE",EDGE,{"disambiguationData":[OSD([sQuery(id+"F1.wireOp",EDGE,"E24.MirrorCS")])],"isStart":false});
            var Q64;
            Q64=makeQuery(id+"F3.opExtrude","CAP_EDGE",EDGE,{"disambiguationData":[OSD([sQuery(id+"F1.wireOp",EDGE,"E31.MirrorCS")])],"isStart":false});
            var Q65;
            Q65=makeQuery(id+"F3.opExtrude","CAP_EDGE",EDGE,{"disambiguationData":[OSD([sQuery(id+"F1.wireOp",EDGE,"E329.MirrorCS")])],"isStart":false});
            var Q66;
            Q66=makeQuery(id+"F3.opExtrude","CAP_EDGE",EDGE,{"disambiguationData":[OSD([sQuery(id+"F1.wireOp",EDGE,"E328.MirrorCS")])],"isStart":false});
            var Q67;
            Q67=makeQuery(id+"F3.opExtrude","CAP_EDGE",EDGE,{"disambiguationData":[OSD([sQuery(id+"F1.wireOp",EDGE,"E194.MirrorCS")])],"isStart":false});
            var Q68;
            Q68=makeQuery(id+"F3.opExtrude","CAP_EDGE",EDGE,{"disambiguationData":[OSD([sQuery(id+"F1.wireOp",EDGE,"E275.MirrorCS")])],"isStart":false});
            var Q69;
            Q69=makeQuery(id+"F3.opExtrude","CAP_EDGE",EDGE,{"disambiguationData":[OSD([sQuery(id+"F1.wireOp",EDGE,"E298.MirrorCS")])],"isStart":false});
            var Q70;
            Q70=makeQuery(id+"F3.opExtrude","CAP_EDGE",EDGE,{"disambiguationData":[OSD([sQuery(id+"F1.wireOp",EDGE,"E199.MirrorCS")])],"isStart":false});
            var Q71;
            Q71=makeQuery(id+"F3.opExtrude","CAP_EDGE",EDGE,{"disambiguationData":[OSD([sQuery(id+"F1.wireOp",EDGE,"E42.MirrorCS")])],"isStart":false});
            var Q72;
            Q72=makeQuery(id+"F3.opExtrude","CAP_EDGE",EDGE,{"disambiguationData":[OSD([sQuery(id+"F1.wireOp",EDGE,"E140.MirrorCS")])],"isStart":false});
            var Q73;
            Q73=makeQuery(id+"F3.opExtrude","CAP_EDGE",EDGE,{"disambiguationData":[OSD([sQuery(id+"F1.wireOp",EDGE,"E163.MirrorCS")])],"isStart":false});
            fillet(context, id + "F6", {"entities" : qUnion([Q0, Q1, Q2, Q3, Q4, Q5, Q6, Q7, Q8, Q9, Q10, Q11, Q12, Q13, Q14, Q15, Q16, Q17, Q18, Q19, Q20, Q21, Q22, Q23, Q24, Q25, Q26, Q27, Q28, Q29, Q30, Q31, Q32, Q33, Q34, Q35, Q36, Q37, Q38, Q39, Q40, Q41, Q42, Q43, Q44, Q45, Q46, Q47, Q48, Q49, Q50, Q51, Q52, Q53, Q54, Q55, Q56, Q57, Q58, Q59, Q60, Q61, Q62, Q63, Q64, Q65, Q66, Q67, Q68, Q69, Q70, Q71, Q72, Q73]), "tangentPropagation" : true, "radius" : 1.5 * mm, "defaultsChanged" : false, "vertexSettings" : [], "allowEdgeOverflow" : false});
        }
    });
